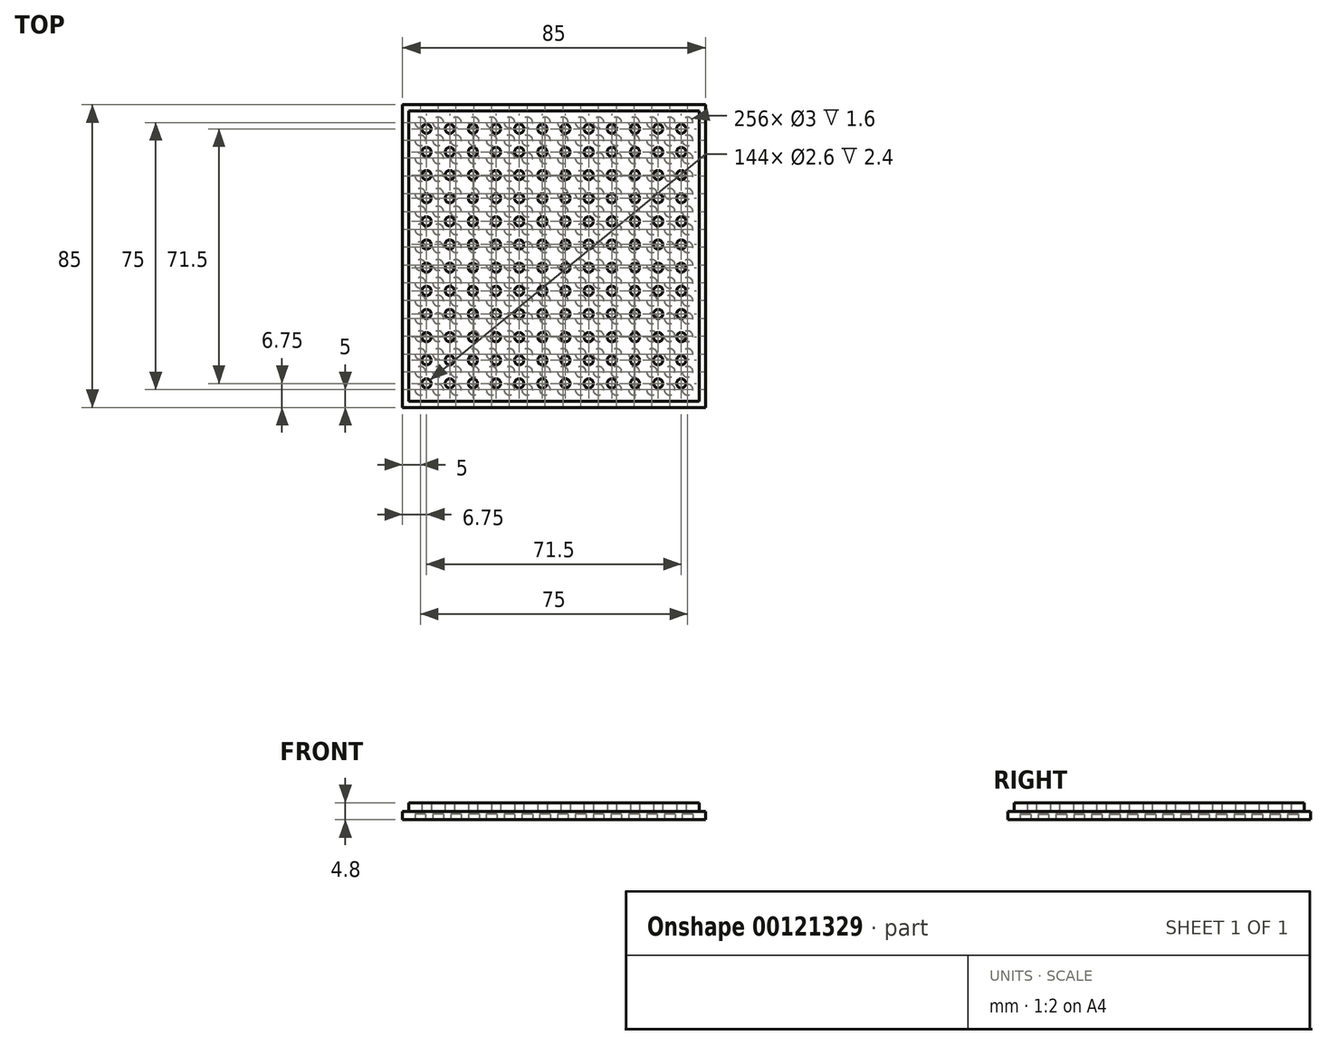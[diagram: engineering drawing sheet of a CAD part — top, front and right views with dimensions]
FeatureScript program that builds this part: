
annotation { "Feature Type Name" : "Feature", "Feature Type Description" : "" }
export const myFeature = defineFeature(function(context is Context, id is Id, definition is map)
    precondition{}
    {
        {
            var Q0;
            Q0=qCreatedBy(makeId("Top.planeOp"),FACE);
            var sketch = newSketch(context, id + "F0", { "sketchPlane" : qUnion([Q0])});
            skLineSegment(sketch, "E0.bottom", {"start": v(2.5, -2.5) * mm, "end": v(-2.5, -2.5) * mm, "construction": true});
            skLineSegment(sketch, "E0.top", {"start": v(2.5, 2.5) * mm, "end": v(-2.5, 2.5) * mm, "construction": true});
            skLineSegment(sketch, "E0.left", {"start": v(2.5, -2.5) * mm, "end": v(2.5, 2.5) * mm, "construction": true});
            skLineSegment(sketch, "E0.right", {"start": v(-2.5, -2.5) * mm, "end": v(-2.5, 2.5) * mm, "construction": true});
            skPoint(sketch, "E0.middle", {"position": v(0, 0) * mm});
            skCircle(sketch, "E1", {"center": v(-2.5, 2.5) * mm, "radius": 1.5 * mm});
            skCircle(sketch, "E2", {"center": v(2.5, 2.5) * mm, "radius": 1.5 * mm});
            skCircle(sketch, "E3", {"center": v(2.5, -2.5) * mm, "radius": 1.5 * mm});
            skCircle(sketch, "E4", {"center": v(-2.5, -2.5) * mm, "radius": 1.5 * mm});
            skPoint(sketch, "E5.0.1.0", {"position": v(0, 10) * mm});
            skLineSegment(sketch, "E5.0.1.1", {"start": v(-2.5, 7.5) * mm, "end": v(-2.5, 12.5) * mm, "construction": true});
            skLineSegment(sketch, "E5.0.1.2", {"start": v(2.5, 7.5) * mm, "end": v(2.5, 12.5) * mm, "construction": true});
            skLineSegment(sketch, "E5.0.1.3", {"start": v(2.5, 7.5) * mm, "end": v(-2.5, 7.5) * mm, "construction": true});
            skLineSegment(sketch, "E5.0.1.4", {"start": v(2.5, 12.5) * mm, "end": v(-2.5, 12.5) * mm, "construction": true});
            skCircle(sketch, "E5.0.1.5", {"center": v(-2.5, 7.5) * mm, "radius": 1.5 * mm});
            skCircle(sketch, "E5.0.1.6", {"center": v(2.5, 7.5) * mm, "radius": 1.5 * mm});
            skCircle(sketch, "E5.0.1.7", {"center": v(2.5, 12.5) * mm, "radius": 1.5 * mm});
            skCircle(sketch, "E5.0.1.8", {"center": v(-2.5, 12.5) * mm, "radius": 1.5 * mm});
            skPoint(sketch, "E5.0.2.0", {"position": v(0, 20) * mm});
            skLineSegment(sketch, "E5.0.2.1", {"start": v(-2.5, 17.5) * mm, "end": v(-2.5, 22.5) * mm, "construction": true});
            skLineSegment(sketch, "E5.0.2.2", {"start": v(2.5, 17.5) * mm, "end": v(2.5, 22.5) * mm, "construction": true});
            skLineSegment(sketch, "E5.0.2.3", {"start": v(2.5, 17.5) * mm, "end": v(-2.5, 17.5) * mm, "construction": true});
            skLineSegment(sketch, "E5.0.2.4", {"start": v(2.5, 22.5) * mm, "end": v(-2.5, 22.5) * mm, "construction": true});
            skCircle(sketch, "E5.0.2.5", {"center": v(-2.5, 17.5) * mm, "radius": 1.5 * mm});
            skCircle(sketch, "E5.0.2.6", {"center": v(2.5, 17.5) * mm, "radius": 1.5 * mm});
            skCircle(sketch, "E5.0.2.7", {"center": v(2.5, 22.5) * mm, "radius": 1.5 * mm});
            skCircle(sketch, "E5.0.2.8", {"center": v(-2.5, 22.5) * mm, "radius": 1.5 * mm});
            skPoint(sketch, "E5.0.3.0", {"position": v(0, 30) * mm});
            skLineSegment(sketch, "E5.0.3.1", {"start": v(-2.5, 27.5) * mm, "end": v(-2.5, 32.5) * mm, "construction": true});
            skLineSegment(sketch, "E5.0.3.2", {"start": v(2.5, 27.5) * mm, "end": v(2.5, 32.5) * mm, "construction": true});
            skLineSegment(sketch, "E5.0.3.3", {"start": v(2.5, 27.5) * mm, "end": v(-2.5, 27.5) * mm, "construction": true});
            skLineSegment(sketch, "E5.0.3.4", {"start": v(2.5, 32.5) * mm, "end": v(-2.5, 32.5) * mm, "construction": true});
            skCircle(sketch, "E5.0.3.5", {"center": v(-2.5, 27.5) * mm, "radius": 1.5 * mm});
            skCircle(sketch, "E5.0.3.6", {"center": v(2.5, 27.5) * mm, "radius": 1.5 * mm});
            skCircle(sketch, "E5.0.3.7", {"center": v(2.5, 32.5) * mm, "radius": 1.5 * mm});
            skCircle(sketch, "E5.0.3.8", {"center": v(-2.5, 32.5) * mm, "radius": 1.5 * mm});
            skPoint(sketch, "E5.0.4.0", {"position": v(0, 40) * mm});
            skLineSegment(sketch, "E5.0.4.1", {"start": v(-2.5, 37.5) * mm, "end": v(-2.5, 42.5) * mm, "construction": true});
            skLineSegment(sketch, "E5.0.4.2", {"start": v(2.5, 37.5) * mm, "end": v(2.5, 42.5) * mm, "construction": true});
            skLineSegment(sketch, "E5.0.4.3", {"start": v(2.5, 37.5) * mm, "end": v(-2.5, 37.5) * mm, "construction": true});
            skLineSegment(sketch, "E5.0.4.4", {"start": v(2.5, 42.5) * mm, "end": v(-2.5, 42.5) * mm, "construction": true});
            skCircle(sketch, "E5.0.4.5", {"center": v(-2.5, 37.5) * mm, "radius": 1.5 * mm});
            skCircle(sketch, "E5.0.4.6", {"center": v(2.5, 37.5) * mm, "radius": 1.5 * mm});
            skCircle(sketch, "E5.0.4.7", {"center": v(2.5, 42.5) * mm, "radius": 1.5 * mm});
            skCircle(sketch, "E5.0.4.8", {"center": v(-2.5, 42.5) * mm, "radius": 1.5 * mm});
            skPoint(sketch, "E5.0.5.0", {"position": v(0, 50) * mm});
            skLineSegment(sketch, "E5.0.5.1", {"start": v(-2.5, 47.5) * mm, "end": v(-2.5, 52.5) * mm, "construction": true});
            skLineSegment(sketch, "E5.0.5.2", {"start": v(2.5, 47.5) * mm, "end": v(2.5, 52.5) * mm, "construction": true});
            skLineSegment(sketch, "E5.0.5.3", {"start": v(2.5, 47.5) * mm, "end": v(-2.5, 47.5) * mm, "construction": true});
            skLineSegment(sketch, "E5.0.5.4", {"start": v(2.5, 52.5) * mm, "end": v(-2.5, 52.5) * mm, "construction": true});
            skCircle(sketch, "E5.0.5.5", {"center": v(-2.5, 47.5) * mm, "radius": 1.5 * mm});
            skCircle(sketch, "E5.0.5.6", {"center": v(2.5, 47.5) * mm, "radius": 1.5 * mm});
            skCircle(sketch, "E5.0.5.7", {"center": v(2.5, 52.5) * mm, "radius": 1.5 * mm});
            skCircle(sketch, "E5.0.5.8", {"center": v(-2.5, 52.5) * mm, "radius": 1.5 * mm});
            skPoint(sketch, "E5.1.0.0", {"position": v(10, 0) * mm});
            skLineSegment(sketch, "E5.1.0.1", {"start": v(7.5, -2.5) * mm, "end": v(7.5, 2.5) * mm, "construction": true});
            skLineSegment(sketch, "E5.1.0.2", {"start": v(12.5, -2.5) * mm, "end": v(12.5, 2.5) * mm, "construction": true});
            skLineSegment(sketch, "E5.1.0.3", {"start": v(12.5, -2.5) * mm, "end": v(7.5, -2.5) * mm, "construction": true});
            skLineSegment(sketch, "E5.1.0.4", {"start": v(12.5, 2.5) * mm, "end": v(7.5, 2.5) * mm, "construction": true});
            skCircle(sketch, "E5.1.0.5", {"center": v(7.5, -2.5) * mm, "radius": 1.5 * mm});
            skCircle(sketch, "E5.1.0.6", {"center": v(12.5, -2.5) * mm, "radius": 1.5 * mm});
            skCircle(sketch, "E5.1.0.7", {"center": v(12.5, 2.5) * mm, "radius": 1.5 * mm});
            skCircle(sketch, "E5.1.0.8", {"center": v(7.5, 2.5) * mm, "radius": 1.5 * mm});
            skPoint(sketch, "E5.1.1.0", {"position": v(10, 10) * mm});
            skLineSegment(sketch, "E5.1.1.1", {"start": v(7.5, 7.5) * mm, "end": v(7.5, 12.5) * mm, "construction": true});
            skLineSegment(sketch, "E5.1.1.2", {"start": v(12.5, 7.5) * mm, "end": v(12.5, 12.5) * mm, "construction": true});
            skLineSegment(sketch, "E5.1.1.3", {"start": v(12.5, 7.5) * mm, "end": v(7.5, 7.5) * mm, "construction": true});
            skLineSegment(sketch, "E5.1.1.4", {"start": v(12.5, 12.5) * mm, "end": v(7.5, 12.5) * mm, "construction": true});
            skCircle(sketch, "E5.1.1.5", {"center": v(7.5, 7.5) * mm, "radius": 1.5 * mm});
            skCircle(sketch, "E5.1.1.6", {"center": v(12.5, 7.5) * mm, "radius": 1.5 * mm});
            skCircle(sketch, "E5.1.1.7", {"center": v(12.5, 12.5) * mm, "radius": 1.5 * mm});
            skCircle(sketch, "E5.1.1.8", {"center": v(7.5, 12.5) * mm, "radius": 1.5 * mm});
            skPoint(sketch, "E5.1.2.0", {"position": v(10, 20) * mm});
            skLineSegment(sketch, "E5.1.2.1", {"start": v(7.5, 17.5) * mm, "end": v(7.5, 22.5) * mm, "construction": true});
            skLineSegment(sketch, "E5.1.2.2", {"start": v(12.5, 17.5) * mm, "end": v(12.5, 22.5) * mm, "construction": true});
            skLineSegment(sketch, "E5.1.2.3", {"start": v(12.5, 17.5) * mm, "end": v(7.5, 17.5) * mm, "construction": true});
            skLineSegment(sketch, "E5.1.2.4", {"start": v(12.5, 22.5) * mm, "end": v(7.5, 22.5) * mm, "construction": true});
            skCircle(sketch, "E5.1.2.5", {"center": v(7.5, 17.5) * mm, "radius": 1.5 * mm});
            skCircle(sketch, "E5.1.2.6", {"center": v(12.5, 17.5) * mm, "radius": 1.5 * mm});
            skCircle(sketch, "E5.1.2.7", {"center": v(12.5, 22.5) * mm, "radius": 1.5 * mm});
            skCircle(sketch, "E5.1.2.8", {"center": v(7.5, 22.5) * mm, "radius": 1.5 * mm});
            skPoint(sketch, "E5.1.3.0", {"position": v(10, 30) * mm});
            skLineSegment(sketch, "E5.1.3.1", {"start": v(7.5, 27.5) * mm, "end": v(7.5, 32.5) * mm, "construction": true});
            skLineSegment(sketch, "E5.1.3.2", {"start": v(12.5, 27.5) * mm, "end": v(12.5, 32.5) * mm, "construction": true});
            skLineSegment(sketch, "E5.1.3.3", {"start": v(12.5, 27.5) * mm, "end": v(7.5, 27.5) * mm, "construction": true});
            skLineSegment(sketch, "E5.1.3.4", {"start": v(12.5, 32.5) * mm, "end": v(7.5, 32.5) * mm, "construction": true});
            skCircle(sketch, "E5.1.3.5", {"center": v(7.5, 27.5) * mm, "radius": 1.5 * mm});
            skCircle(sketch, "E5.1.3.6", {"center": v(12.5, 27.5) * mm, "radius": 1.5 * mm});
            skCircle(sketch, "E5.1.3.7", {"center": v(12.5, 32.5) * mm, "radius": 1.5 * mm});
            skCircle(sketch, "E5.1.3.8", {"center": v(7.5, 32.5) * mm, "radius": 1.5 * mm});
            skPoint(sketch, "E5.1.4.0", {"position": v(10, 40) * mm});
            skLineSegment(sketch, "E5.1.4.1", {"start": v(7.5, 37.5) * mm, "end": v(7.5, 42.5) * mm, "construction": true});
            skLineSegment(sketch, "E5.1.4.2", {"start": v(12.5, 37.5) * mm, "end": v(12.5, 42.5) * mm, "construction": true});
            skLineSegment(sketch, "E5.1.4.3", {"start": v(12.5, 37.5) * mm, "end": v(7.5, 37.5) * mm, "construction": true});
            skLineSegment(sketch, "E5.1.4.4", {"start": v(12.5, 42.5) * mm, "end": v(7.5, 42.5) * mm, "construction": true});
            skCircle(sketch, "E5.1.4.5", {"center": v(7.5, 37.5) * mm, "radius": 1.5 * mm});
            skCircle(sketch, "E5.1.4.6", {"center": v(12.5, 37.5) * mm, "radius": 1.5 * mm});
            skCircle(sketch, "E5.1.4.7", {"center": v(12.5, 42.5) * mm, "radius": 1.5 * mm});
            skCircle(sketch, "E5.1.4.8", {"center": v(7.5, 42.5) * mm, "radius": 1.5 * mm});
            skPoint(sketch, "E5.1.5.0", {"position": v(10, 50) * mm});
            skLineSegment(sketch, "E5.1.5.1", {"start": v(7.5, 47.5) * mm, "end": v(7.5, 52.5) * mm, "construction": true});
            skLineSegment(sketch, "E5.1.5.2", {"start": v(12.5, 47.5) * mm, "end": v(12.5, 52.5) * mm, "construction": true});
            skLineSegment(sketch, "E5.1.5.3", {"start": v(12.5, 47.5) * mm, "end": v(7.5, 47.5) * mm, "construction": true});
            skLineSegment(sketch, "E5.1.5.4", {"start": v(12.5, 52.5) * mm, "end": v(7.5, 52.5) * mm, "construction": true});
            skCircle(sketch, "E5.1.5.5", {"center": v(7.5, 47.5) * mm, "radius": 1.5 * mm});
            skCircle(sketch, "E5.1.5.6", {"center": v(12.5, 47.5) * mm, "radius": 1.5 * mm});
            skCircle(sketch, "E5.1.5.7", {"center": v(12.5, 52.5) * mm, "radius": 1.5 * mm});
            skCircle(sketch, "E5.1.5.8", {"center": v(7.5, 52.5) * mm, "radius": 1.5 * mm});
            skPoint(sketch, "E5.2.0.0", {"position": v(20, 0) * mm});
            skLineSegment(sketch, "E5.2.0.1", {"start": v(17.5, -2.5) * mm, "end": v(17.5, 2.5) * mm, "construction": true});
            skLineSegment(sketch, "E5.2.0.2", {"start": v(22.5, -2.5) * mm, "end": v(22.5, 2.5) * mm, "construction": true});
            skLineSegment(sketch, "E5.2.0.3", {"start": v(22.5, -2.5) * mm, "end": v(17.5, -2.5) * mm, "construction": true});
            skLineSegment(sketch, "E5.2.0.4", {"start": v(22.5, 2.5) * mm, "end": v(17.5, 2.5) * mm, "construction": true});
            skCircle(sketch, "E5.2.0.5", {"center": v(17.5, -2.5) * mm, "radius": 1.5 * mm});
            skCircle(sketch, "E5.2.0.6", {"center": v(22.5, -2.5) * mm, "radius": 1.5 * mm});
            skCircle(sketch, "E5.2.0.7", {"center": v(22.5, 2.5) * mm, "radius": 1.5 * mm});
            skCircle(sketch, "E5.2.0.8", {"center": v(17.5, 2.5) * mm, "radius": 1.5 * mm});
            skPoint(sketch, "E5.2.1.0", {"position": v(20, 10) * mm});
            skLineSegment(sketch, "E5.2.1.1", {"start": v(17.5, 7.5) * mm, "end": v(17.5, 12.5) * mm, "construction": true});
            skLineSegment(sketch, "E5.2.1.2", {"start": v(22.5, 7.5) * mm, "end": v(22.5, 12.5) * mm, "construction": true});
            skLineSegment(sketch, "E5.2.1.3", {"start": v(22.5, 7.5) * mm, "end": v(17.5, 7.5) * mm, "construction": true});
            skLineSegment(sketch, "E5.2.1.4", {"start": v(22.5, 12.5) * mm, "end": v(17.5, 12.5) * mm, "construction": true});
            skCircle(sketch, "E5.2.1.5", {"center": v(17.5, 7.5) * mm, "radius": 1.5 * mm});
            skCircle(sketch, "E5.2.1.6", {"center": v(22.5, 7.5) * mm, "radius": 1.5 * mm});
            skCircle(sketch, "E5.2.1.7", {"center": v(22.5, 12.5) * mm, "radius": 1.5 * mm});
            skCircle(sketch, "E5.2.1.8", {"center": v(17.5, 12.5) * mm, "radius": 1.5 * mm});
            skPoint(sketch, "E5.2.2.0", {"position": v(20, 20) * mm});
            skLineSegment(sketch, "E5.2.2.1", {"start": v(17.5, 17.5) * mm, "end": v(17.5, 22.5) * mm, "construction": true});
            skLineSegment(sketch, "E5.2.2.2", {"start": v(22.5, 17.5) * mm, "end": v(22.5, 22.5) * mm, "construction": true});
            skLineSegment(sketch, "E5.2.2.3", {"start": v(22.5, 17.5) * mm, "end": v(17.5, 17.5) * mm, "construction": true});
            skLineSegment(sketch, "E5.2.2.4", {"start": v(22.5, 22.5) * mm, "end": v(17.5, 22.5) * mm, "construction": true});
            skCircle(sketch, "E5.2.2.5", {"center": v(17.5, 17.5) * mm, "radius": 1.5 * mm});
            skCircle(sketch, "E5.2.2.6", {"center": v(22.5, 17.5) * mm, "radius": 1.5 * mm});
            skCircle(sketch, "E5.2.2.7", {"center": v(22.5, 22.5) * mm, "radius": 1.5 * mm});
            skCircle(sketch, "E5.2.2.8", {"center": v(17.5, 22.5) * mm, "radius": 1.5 * mm});
            skPoint(sketch, "E5.2.3.0", {"position": v(20, 30) * mm});
            skLineSegment(sketch, "E5.2.3.1", {"start": v(17.5, 27.5) * mm, "end": v(17.5, 32.5) * mm, "construction": true});
            skLineSegment(sketch, "E5.2.3.2", {"start": v(22.5, 27.5) * mm, "end": v(22.5, 32.5) * mm, "construction": true});
            skLineSegment(sketch, "E5.2.3.3", {"start": v(22.5, 27.5) * mm, "end": v(17.5, 27.5) * mm, "construction": true});
            skLineSegment(sketch, "E5.2.3.4", {"start": v(22.5, 32.5) * mm, "end": v(17.5, 32.5) * mm, "construction": true});
            skCircle(sketch, "E5.2.3.5", {"center": v(17.5, 27.5) * mm, "radius": 1.5 * mm});
            skCircle(sketch, "E5.2.3.6", {"center": v(22.5, 27.5) * mm, "radius": 1.5 * mm});
            skCircle(sketch, "E5.2.3.7", {"center": v(22.5, 32.5) * mm, "radius": 1.5 * mm});
            skCircle(sketch, "E5.2.3.8", {"center": v(17.5, 32.5) * mm, "radius": 1.5 * mm});
            skPoint(sketch, "E5.2.4.0", {"position": v(20, 40) * mm});
            skLineSegment(sketch, "E5.2.4.1", {"start": v(17.5, 37.5) * mm, "end": v(17.5, 42.5) * mm, "construction": true});
            skLineSegment(sketch, "E5.2.4.2", {"start": v(22.5, 37.5) * mm, "end": v(22.5, 42.5) * mm, "construction": true});
            skLineSegment(sketch, "E5.2.4.3", {"start": v(22.5, 37.5) * mm, "end": v(17.5, 37.5) * mm, "construction": true});
            skLineSegment(sketch, "E5.2.4.4", {"start": v(22.5, 42.5) * mm, "end": v(17.5, 42.5) * mm, "construction": true});
            skCircle(sketch, "E5.2.4.5", {"center": v(17.5, 37.5) * mm, "radius": 1.5 * mm});
            skCircle(sketch, "E5.2.4.6", {"center": v(22.5, 37.5) * mm, "radius": 1.5 * mm});
            skCircle(sketch, "E5.2.4.7", {"center": v(22.5, 42.5) * mm, "radius": 1.5 * mm});
            skCircle(sketch, "E5.2.4.8", {"center": v(17.5, 42.5) * mm, "radius": 1.5 * mm});
            skPoint(sketch, "E5.2.5.0", {"position": v(20, 50) * mm});
            skLineSegment(sketch, "E5.2.5.1", {"start": v(17.5, 47.5) * mm, "end": v(17.5, 52.5) * mm, "construction": true});
            skLineSegment(sketch, "E5.2.5.2", {"start": v(22.5, 47.5) * mm, "end": v(22.5, 52.5) * mm, "construction": true});
            skLineSegment(sketch, "E5.2.5.3", {"start": v(22.5, 47.5) * mm, "end": v(17.5, 47.5) * mm, "construction": true});
            skLineSegment(sketch, "E5.2.5.4", {"start": v(22.5, 52.5) * mm, "end": v(17.5, 52.5) * mm, "construction": true});
            skCircle(sketch, "E5.2.5.5", {"center": v(17.5, 47.5) * mm, "radius": 1.5 * mm});
            skCircle(sketch, "E5.2.5.6", {"center": v(22.5, 47.5) * mm, "radius": 1.5 * mm});
            skCircle(sketch, "E5.2.5.7", {"center": v(22.5, 52.5) * mm, "radius": 1.5 * mm});
            skCircle(sketch, "E5.2.5.8", {"center": v(17.5, 52.5) * mm, "radius": 1.5 * mm});
            skPoint(sketch, "E5.3.0.0", {"position": v(30, 0) * mm});
            skLineSegment(sketch, "E5.3.0.1", {"start": v(27.5, -2.5) * mm, "end": v(27.5, 2.5) * mm, "construction": true});
            skLineSegment(sketch, "E5.3.0.2", {"start": v(32.5, -2.5) * mm, "end": v(32.5, 2.5) * mm, "construction": true});
            skLineSegment(sketch, "E5.3.0.3", {"start": v(32.5, -2.5) * mm, "end": v(27.5, -2.5) * mm, "construction": true});
            skLineSegment(sketch, "E5.3.0.4", {"start": v(32.5, 2.5) * mm, "end": v(27.5, 2.5) * mm, "construction": true});
            skCircle(sketch, "E5.3.0.5", {"center": v(27.5, -2.5) * mm, "radius": 1.5 * mm});
            skCircle(sketch, "E5.3.0.6", {"center": v(32.5, -2.5) * mm, "radius": 1.5 * mm});
            skCircle(sketch, "E5.3.0.7", {"center": v(32.5, 2.5) * mm, "radius": 1.5 * mm});
            skCircle(sketch, "E5.3.0.8", {"center": v(27.5, 2.5) * mm, "radius": 1.5 * mm});
            skPoint(sketch, "E5.3.1.0", {"position": v(30, 10) * mm});
            skLineSegment(sketch, "E5.3.1.1", {"start": v(27.5, 7.5) * mm, "end": v(27.5, 12.5) * mm, "construction": true});
            skLineSegment(sketch, "E5.3.1.2", {"start": v(32.5, 7.5) * mm, "end": v(32.5, 12.5) * mm, "construction": true});
            skLineSegment(sketch, "E5.3.1.3", {"start": v(32.5, 7.5) * mm, "end": v(27.5, 7.5) * mm, "construction": true});
            skLineSegment(sketch, "E5.3.1.4", {"start": v(32.5, 12.5) * mm, "end": v(27.5, 12.5) * mm, "construction": true});
            skCircle(sketch, "E5.3.1.5", {"center": v(27.5, 7.5) * mm, "radius": 1.5 * mm});
            skCircle(sketch, "E5.3.1.6", {"center": v(32.5, 7.5) * mm, "radius": 1.5 * mm});
            skCircle(sketch, "E5.3.1.7", {"center": v(32.5, 12.5) * mm, "radius": 1.5 * mm});
            skCircle(sketch, "E5.3.1.8", {"center": v(27.5, 12.5) * mm, "radius": 1.5 * mm});
            skPoint(sketch, "E5.3.2.0", {"position": v(30, 20) * mm});
            skLineSegment(sketch, "E5.3.2.1", {"start": v(27.5, 17.5) * mm, "end": v(27.5, 22.5) * mm, "construction": true});
            skLineSegment(sketch, "E5.3.2.2", {"start": v(32.5, 17.5) * mm, "end": v(32.5, 22.5) * mm, "construction": true});
            skLineSegment(sketch, "E5.3.2.3", {"start": v(32.5, 17.5) * mm, "end": v(27.5, 17.5) * mm, "construction": true});
            skLineSegment(sketch, "E5.3.2.4", {"start": v(32.5, 22.5) * mm, "end": v(27.5, 22.5) * mm, "construction": true});
            skCircle(sketch, "E5.3.2.5", {"center": v(27.5, 17.5) * mm, "radius": 1.5 * mm});
            skCircle(sketch, "E5.3.2.6", {"center": v(32.5, 17.5) * mm, "radius": 1.5 * mm});
            skCircle(sketch, "E5.3.2.7", {"center": v(32.5, 22.5) * mm, "radius": 1.5 * mm});
            skCircle(sketch, "E5.3.2.8", {"center": v(27.5, 22.5) * mm, "radius": 1.5 * mm});
            skPoint(sketch, "E5.3.3.0", {"position": v(30, 30) * mm});
            skLineSegment(sketch, "E5.3.3.1", {"start": v(27.5, 27.5) * mm, "end": v(27.5, 32.5) * mm, "construction": true});
            skLineSegment(sketch, "E5.3.3.2", {"start": v(32.5, 27.5) * mm, "end": v(32.5, 32.5) * mm, "construction": true});
            skLineSegment(sketch, "E5.3.3.3", {"start": v(32.5, 27.5) * mm, "end": v(27.5, 27.5) * mm, "construction": true});
            skLineSegment(sketch, "E5.3.3.4", {"start": v(32.5, 32.5) * mm, "end": v(27.5, 32.5) * mm, "construction": true});
            skCircle(sketch, "E5.3.3.5", {"center": v(27.5, 27.5) * mm, "radius": 1.5 * mm});
            skCircle(sketch, "E5.3.3.6", {"center": v(32.5, 27.5) * mm, "radius": 1.5 * mm});
            skCircle(sketch, "E5.3.3.7", {"center": v(32.5, 32.5) * mm, "radius": 1.5 * mm});
            skCircle(sketch, "E5.3.3.8", {"center": v(27.5, 32.5) * mm, "radius": 1.5 * mm});
            skPoint(sketch, "E5.3.4.0", {"position": v(30, 40) * mm});
            skLineSegment(sketch, "E5.3.4.1", {"start": v(27.5, 37.5) * mm, "end": v(27.5, 42.5) * mm, "construction": true});
            skLineSegment(sketch, "E5.3.4.2", {"start": v(32.5, 37.5) * mm, "end": v(32.5, 42.5) * mm, "construction": true});
            skLineSegment(sketch, "E5.3.4.3", {"start": v(32.5, 37.5) * mm, "end": v(27.5, 37.5) * mm, "construction": true});
            skLineSegment(sketch, "E5.3.4.4", {"start": v(32.5, 42.5) * mm, "end": v(27.5, 42.5) * mm, "construction": true});
            skCircle(sketch, "E5.3.4.5", {"center": v(27.5, 37.5) * mm, "radius": 1.5 * mm});
            skCircle(sketch, "E5.3.4.6", {"center": v(32.5, 37.5) * mm, "radius": 1.5 * mm});
            skCircle(sketch, "E5.3.4.7", {"center": v(32.5, 42.5) * mm, "radius": 1.5 * mm});
            skCircle(sketch, "E5.3.4.8", {"center": v(27.5, 42.5) * mm, "radius": 1.5 * mm});
            skPoint(sketch, "E5.3.5.0", {"position": v(30, 50) * mm});
            skLineSegment(sketch, "E5.3.5.1", {"start": v(27.5, 47.5) * mm, "end": v(27.5, 52.5) * mm, "construction": true});
            skLineSegment(sketch, "E5.3.5.2", {"start": v(32.5, 47.5) * mm, "end": v(32.5, 52.5) * mm, "construction": true});
            skLineSegment(sketch, "E5.3.5.3", {"start": v(32.5, 47.5) * mm, "end": v(27.5, 47.5) * mm, "construction": true});
            skLineSegment(sketch, "E5.3.5.4", {"start": v(32.5, 52.5) * mm, "end": v(27.5, 52.5) * mm, "construction": true});
            skCircle(sketch, "E5.3.5.5", {"center": v(27.5, 47.5) * mm, "radius": 1.5 * mm});
            skCircle(sketch, "E5.3.5.6", {"center": v(32.5, 47.5) * mm, "radius": 1.5 * mm});
            skCircle(sketch, "E5.3.5.7", {"center": v(32.5, 52.5) * mm, "radius": 1.5 * mm});
            skCircle(sketch, "E5.3.5.8", {"center": v(27.5, 52.5) * mm, "radius": 1.5 * mm});
            skPoint(sketch, "E5.4.0.0", {"position": v(40, 0) * mm});
            skLineSegment(sketch, "E5.4.0.1", {"start": v(37.5, -2.5) * mm, "end": v(37.5, 2.5) * mm, "construction": true});
            skLineSegment(sketch, "E5.4.0.2", {"start": v(42.5, -2.5) * mm, "end": v(42.5, 2.5) * mm, "construction": true});
            skLineSegment(sketch, "E5.4.0.3", {"start": v(42.5, -2.5) * mm, "end": v(37.5, -2.5) * mm, "construction": true});
            skLineSegment(sketch, "E5.4.0.4", {"start": v(42.5, 2.5) * mm, "end": v(37.5, 2.5) * mm, "construction": true});
            skCircle(sketch, "E5.4.0.5", {"center": v(37.5, -2.5) * mm, "radius": 1.5 * mm});
            skCircle(sketch, "E5.4.0.6", {"center": v(42.5, -2.5) * mm, "radius": 1.5 * mm});
            skCircle(sketch, "E5.4.0.7", {"center": v(42.5, 2.5) * mm, "radius": 1.5 * mm});
            skCircle(sketch, "E5.4.0.8", {"center": v(37.5, 2.5) * mm, "radius": 1.5 * mm});
            skPoint(sketch, "E5.4.1.0", {"position": v(40, 10) * mm});
            skLineSegment(sketch, "E5.4.1.1", {"start": v(37.5, 7.5) * mm, "end": v(37.5, 12.5) * mm, "construction": true});
            skLineSegment(sketch, "E5.4.1.2", {"start": v(42.5, 7.5) * mm, "end": v(42.5, 12.5) * mm, "construction": true});
            skLineSegment(sketch, "E5.4.1.3", {"start": v(42.5, 7.5) * mm, "end": v(37.5, 7.5) * mm, "construction": true});
            skLineSegment(sketch, "E5.4.1.4", {"start": v(42.5, 12.5) * mm, "end": v(37.5, 12.5) * mm, "construction": true});
            skCircle(sketch, "E5.4.1.5", {"center": v(37.5, 7.5) * mm, "radius": 1.5 * mm});
            skCircle(sketch, "E5.4.1.6", {"center": v(42.5, 7.5) * mm, "radius": 1.5 * mm});
            skCircle(sketch, "E5.4.1.7", {"center": v(42.5, 12.5) * mm, "radius": 1.5 * mm});
            skCircle(sketch, "E5.4.1.8", {"center": v(37.5, 12.5) * mm, "radius": 1.5 * mm});
            skPoint(sketch, "E5.4.2.0", {"position": v(40, 20) * mm});
            skLineSegment(sketch, "E5.4.2.1", {"start": v(37.5, 17.5) * mm, "end": v(37.5, 22.5) * mm, "construction": true});
            skLineSegment(sketch, "E5.4.2.2", {"start": v(42.5, 17.5) * mm, "end": v(42.5, 22.5) * mm, "construction": true});
            skLineSegment(sketch, "E5.4.2.3", {"start": v(42.5, 17.5) * mm, "end": v(37.5, 17.5) * mm, "construction": true});
            skLineSegment(sketch, "E5.4.2.4", {"start": v(42.5, 22.5) * mm, "end": v(37.5, 22.5) * mm, "construction": true});
            skCircle(sketch, "E5.4.2.5", {"center": v(37.5, 17.5) * mm, "radius": 1.5 * mm});
            skCircle(sketch, "E5.4.2.6", {"center": v(42.5, 17.5) * mm, "radius": 1.5 * mm});
            skCircle(sketch, "E5.4.2.7", {"center": v(42.5, 22.5) * mm, "radius": 1.5 * mm});
            skCircle(sketch, "E5.4.2.8", {"center": v(37.5, 22.5) * mm, "radius": 1.5 * mm});
            skPoint(sketch, "E5.4.3.0", {"position": v(40, 30) * mm});
            skLineSegment(sketch, "E5.4.3.1", {"start": v(37.5, 27.5) * mm, "end": v(37.5, 32.5) * mm, "construction": true});
            skLineSegment(sketch, "E5.4.3.2", {"start": v(42.5, 27.5) * mm, "end": v(42.5, 32.5) * mm, "construction": true});
            skLineSegment(sketch, "E5.4.3.3", {"start": v(42.5, 27.5) * mm, "end": v(37.5, 27.5) * mm, "construction": true});
            skLineSegment(sketch, "E5.4.3.4", {"start": v(42.5, 32.5) * mm, "end": v(37.5, 32.5) * mm, "construction": true});
            skCircle(sketch, "E5.4.3.5", {"center": v(37.5, 27.5) * mm, "radius": 1.5 * mm});
            skCircle(sketch, "E5.4.3.6", {"center": v(42.5, 27.5) * mm, "radius": 1.5 * mm});
            skCircle(sketch, "E5.4.3.7", {"center": v(42.5, 32.5) * mm, "radius": 1.5 * mm});
            skCircle(sketch, "E5.4.3.8", {"center": v(37.5, 32.5) * mm, "radius": 1.5 * mm});
            skPoint(sketch, "E5.4.4.0", {"position": v(40, 40) * mm});
            skLineSegment(sketch, "E5.4.4.1", {"start": v(37.5, 37.5) * mm, "end": v(37.5, 42.5) * mm, "construction": true});
            skLineSegment(sketch, "E5.4.4.2", {"start": v(42.5, 37.5) * mm, "end": v(42.5, 42.5) * mm, "construction": true});
            skLineSegment(sketch, "E5.4.4.3", {"start": v(42.5, 37.5) * mm, "end": v(37.5, 37.5) * mm, "construction": true});
            skLineSegment(sketch, "E5.4.4.4", {"start": v(42.5, 42.5) * mm, "end": v(37.5, 42.5) * mm, "construction": true});
            skCircle(sketch, "E5.4.4.5", {"center": v(37.5, 37.5) * mm, "radius": 1.5 * mm});
            skCircle(sketch, "E5.4.4.6", {"center": v(42.5, 37.5) * mm, "radius": 1.5 * mm});
            skCircle(sketch, "E5.4.4.7", {"center": v(42.5, 42.5) * mm, "radius": 1.5 * mm});
            skCircle(sketch, "E5.4.4.8", {"center": v(37.5, 42.5) * mm, "radius": 1.5 * mm});
            skPoint(sketch, "E5.4.5.0", {"position": v(40, 50) * mm});
            skLineSegment(sketch, "E5.4.5.1", {"start": v(37.5, 47.5) * mm, "end": v(37.5, 52.5) * mm, "construction": true});
            skLineSegment(sketch, "E5.4.5.2", {"start": v(42.5, 47.5) * mm, "end": v(42.5, 52.5) * mm, "construction": true});
            skLineSegment(sketch, "E5.4.5.3", {"start": v(42.5, 47.5) * mm, "end": v(37.5, 47.5) * mm, "construction": true});
            skLineSegment(sketch, "E5.4.5.4", {"start": v(42.5, 52.5) * mm, "end": v(37.5, 52.5) * mm, "construction": true});
            skCircle(sketch, "E5.4.5.5", {"center": v(37.5, 47.5) * mm, "radius": 1.5 * mm});
            skCircle(sketch, "E5.4.5.6", {"center": v(42.5, 47.5) * mm, "radius": 1.5 * mm});
            skCircle(sketch, "E5.4.5.7", {"center": v(42.5, 52.5) * mm, "radius": 1.5 * mm});
            skCircle(sketch, "E5.4.5.8", {"center": v(37.5, 52.5) * mm, "radius": 1.5 * mm});
            skPoint(sketch, "E5.5.0.0", {"position": v(50, 0) * mm});
            skLineSegment(sketch, "E5.5.0.1", {"start": v(47.5, -2.5) * mm, "end": v(47.5, 2.5) * mm, "construction": true});
            skLineSegment(sketch, "E5.5.0.2", {"start": v(52.5, -2.5) * mm, "end": v(52.5, 2.5) * mm, "construction": true});
            skLineSegment(sketch, "E5.5.0.3", {"start": v(52.5, -2.5) * mm, "end": v(47.5, -2.5) * mm, "construction": true});
            skLineSegment(sketch, "E5.5.0.4", {"start": v(52.5, 2.5) * mm, "end": v(47.5, 2.5) * mm, "construction": true});
            skCircle(sketch, "E5.5.0.5", {"center": v(47.5, -2.5) * mm, "radius": 1.5 * mm});
            skCircle(sketch, "E5.5.0.6", {"center": v(52.5, -2.5) * mm, "radius": 1.5 * mm});
            skCircle(sketch, "E5.5.0.7", {"center": v(52.5, 2.5) * mm, "radius": 1.5 * mm});
            skCircle(sketch, "E5.5.0.8", {"center": v(47.5, 2.5) * mm, "radius": 1.5 * mm});
            skPoint(sketch, "E5.5.1.0", {"position": v(50, 10) * mm});
            skLineSegment(sketch, "E5.5.1.1", {"start": v(47.5, 7.5) * mm, "end": v(47.5, 12.5) * mm, "construction": true});
            skLineSegment(sketch, "E5.5.1.2", {"start": v(52.5, 7.5) * mm, "end": v(52.5, 12.5) * mm, "construction": true});
            skLineSegment(sketch, "E5.5.1.3", {"start": v(52.5, 7.5) * mm, "end": v(47.5, 7.5) * mm, "construction": true});
            skLineSegment(sketch, "E5.5.1.4", {"start": v(52.5, 12.5) * mm, "end": v(47.5, 12.5) * mm, "construction": true});
            skCircle(sketch, "E5.5.1.5", {"center": v(47.5, 7.5) * mm, "radius": 1.5 * mm});
            skCircle(sketch, "E5.5.1.6", {"center": v(52.5, 7.5) * mm, "radius": 1.5 * mm});
            skCircle(sketch, "E5.5.1.7", {"center": v(52.5, 12.5) * mm, "radius": 1.5 * mm});
            skCircle(sketch, "E5.5.1.8", {"center": v(47.5, 12.5) * mm, "radius": 1.5 * mm});
            skPoint(sketch, "E5.5.2.0", {"position": v(50, 20) * mm});
            skLineSegment(sketch, "E5.5.2.1", {"start": v(47.5, 17.5) * mm, "end": v(47.5, 22.5) * mm, "construction": true});
            skLineSegment(sketch, "E5.5.2.2", {"start": v(52.5, 17.5) * mm, "end": v(52.5, 22.5) * mm, "construction": true});
            skLineSegment(sketch, "E5.5.2.3", {"start": v(52.5, 17.5) * mm, "end": v(47.5, 17.5) * mm, "construction": true});
            skLineSegment(sketch, "E5.5.2.4", {"start": v(52.5, 22.5) * mm, "end": v(47.5, 22.5) * mm, "construction": true});
            skCircle(sketch, "E5.5.2.5", {"center": v(47.5, 17.5) * mm, "radius": 1.5 * mm});
            skCircle(sketch, "E5.5.2.6", {"center": v(52.5, 17.5) * mm, "radius": 1.5 * mm});
            skCircle(sketch, "E5.5.2.7", {"center": v(52.5, 22.5) * mm, "radius": 1.5 * mm});
            skCircle(sketch, "E5.5.2.8", {"center": v(47.5, 22.5) * mm, "radius": 1.5 * mm});
            skPoint(sketch, "E5.5.3.0", {"position": v(50, 30) * mm});
            skLineSegment(sketch, "E5.5.3.1", {"start": v(47.5, 27.5) * mm, "end": v(47.5, 32.5) * mm, "construction": true});
            skLineSegment(sketch, "E5.5.3.2", {"start": v(52.5, 27.5) * mm, "end": v(52.5, 32.5) * mm, "construction": true});
            skLineSegment(sketch, "E5.5.3.3", {"start": v(52.5, 27.5) * mm, "end": v(47.5, 27.5) * mm, "construction": true});
            skLineSegment(sketch, "E5.5.3.4", {"start": v(52.5, 32.5) * mm, "end": v(47.5, 32.5) * mm, "construction": true});
            skCircle(sketch, "E5.5.3.5", {"center": v(47.5, 27.5) * mm, "radius": 1.5 * mm});
            skCircle(sketch, "E5.5.3.6", {"center": v(52.5, 27.5) * mm, "radius": 1.5 * mm});
            skCircle(sketch, "E5.5.3.7", {"center": v(52.5, 32.5) * mm, "radius": 1.5 * mm});
            skCircle(sketch, "E5.5.3.8", {"center": v(47.5, 32.5) * mm, "radius": 1.5 * mm});
            skPoint(sketch, "E5.5.4.0", {"position": v(50, 40) * mm});
            skLineSegment(sketch, "E5.5.4.1", {"start": v(47.5, 37.5) * mm, "end": v(47.5, 42.5) * mm, "construction": true});
            skLineSegment(sketch, "E5.5.4.2", {"start": v(52.5, 37.5) * mm, "end": v(52.5, 42.5) * mm, "construction": true});
            skLineSegment(sketch, "E5.5.4.3", {"start": v(52.5, 37.5) * mm, "end": v(47.5, 37.5) * mm, "construction": true});
            skLineSegment(sketch, "E5.5.4.4", {"start": v(52.5, 42.5) * mm, "end": v(47.5, 42.5) * mm, "construction": true});
            skCircle(sketch, "E5.5.4.5", {"center": v(47.5, 37.5) * mm, "radius": 1.5 * mm});
            skCircle(sketch, "E5.5.4.6", {"center": v(52.5, 37.5) * mm, "radius": 1.5 * mm});
            skCircle(sketch, "E5.5.4.7", {"center": v(52.5, 42.5) * mm, "radius": 1.5 * mm});
            skCircle(sketch, "E5.5.4.8", {"center": v(47.5, 42.5) * mm, "radius": 1.5 * mm});
            skPoint(sketch, "E5.5.5.0", {"position": v(50, 50) * mm});
            skLineSegment(sketch, "E5.5.5.1", {"start": v(47.5, 47.5) * mm, "end": v(47.5, 52.5) * mm, "construction": true});
            skLineSegment(sketch, "E5.5.5.2", {"start": v(52.5, 47.5) * mm, "end": v(52.5, 52.5) * mm, "construction": true});
            skLineSegment(sketch, "E5.5.5.3", {"start": v(52.5, 47.5) * mm, "end": v(47.5, 47.5) * mm, "construction": true});
            skLineSegment(sketch, "E5.5.5.4", {"start": v(52.5, 52.5) * mm, "end": v(47.5, 52.5) * mm, "construction": true});
            skCircle(sketch, "E5.5.5.5", {"center": v(47.5, 47.5) * mm, "radius": 1.5 * mm});
            skCircle(sketch, "E5.5.5.6", {"center": v(52.5, 47.5) * mm, "radius": 1.5 * mm});
            skCircle(sketch, "E5.5.5.7", {"center": v(52.5, 52.5) * mm, "radius": 1.5 * mm});
            skCircle(sketch, "E5.5.5.8", {"center": v(47.5, 52.5) * mm, "radius": 1.5 * mm});
            skLineSegment(sketch, "E5.direction1", {"start": v(-2.5, -2.5) * mm, "end": v(7.5, -2.5) * mm, "construction": true});
            skLineSegment(sketch, "E5.direction2", {"start": v(-2.5, -2.5) * mm, "end": v(-2.5, 7.5) * mm, "construction": true});
            skPoint(sketch, "E6.0.6.0", {"position": v(60, 0) * mm});
            skLineSegment(sketch, "E6.1.6.0", {"start": v(57.5, -2.5) * mm, "end": v(57.5, 2.5) * mm, "construction": true});
            skLineSegment(sketch, "E6.4.6.0", {"start": v(62.5, -2.5) * mm, "end": v(62.5, 2.5) * mm, "construction": true});
            skLineSegment(sketch, "E6.7.6.0", {"start": v(62.5, -2.5) * mm, "end": v(57.5, -2.5) * mm, "construction": true});
            skLineSegment(sketch, "E6.10.6.0", {"start": v(62.5, 2.5) * mm, "end": v(57.5, 2.5) * mm, "construction": true});
            skCircle(sketch, "E6.13.6.0", {"center": v(57.5, -2.5) * mm, "radius": 1.5 * mm});
            skCircle(sketch, "E6.15.6.0", {"center": v(62.5, -2.5) * mm, "radius": 1.5 * mm});
            skCircle(sketch, "E6.17.6.0", {"center": v(62.5, 2.5) * mm, "radius": 1.5 * mm});
            skCircle(sketch, "E6.19.6.0", {"center": v(57.5, 2.5) * mm, "radius": 1.5 * mm});
            skPoint(sketch, "E6.0.6.1", {"position": v(60, 10) * mm});
            skLineSegment(sketch, "E6.1.6.1", {"start": v(57.5, 7.5) * mm, "end": v(57.5, 12.5) * mm, "construction": true});
            skLineSegment(sketch, "E6.4.6.1", {"start": v(62.5, 7.5) * mm, "end": v(62.5, 12.5) * mm, "construction": true});
            skLineSegment(sketch, "E6.7.6.1", {"start": v(62.5, 7.5) * mm, "end": v(57.5, 7.5) * mm, "construction": true});
            skLineSegment(sketch, "E6.10.6.1", {"start": v(62.5, 12.5) * mm, "end": v(57.5, 12.5) * mm, "construction": true});
            skCircle(sketch, "E6.13.6.1", {"center": v(57.5, 7.5) * mm, "radius": 1.5 * mm});
            skCircle(sketch, "E6.15.6.1", {"center": v(62.5, 7.5) * mm, "radius": 1.5 * mm});
            skCircle(sketch, "E6.17.6.1", {"center": v(62.5, 12.5) * mm, "radius": 1.5 * mm});
            skCircle(sketch, "E6.19.6.1", {"center": v(57.5, 12.5) * mm, "radius": 1.5 * mm});
            skPoint(sketch, "E6.0.6.2", {"position": v(60, 20) * mm});
            skLineSegment(sketch, "E6.1.6.2", {"start": v(57.5, 17.5) * mm, "end": v(57.5, 22.5) * mm, "construction": true});
            skLineSegment(sketch, "E6.4.6.2", {"start": v(62.5, 17.5) * mm, "end": v(62.5, 22.5) * mm, "construction": true});
            skLineSegment(sketch, "E6.7.6.2", {"start": v(62.5, 17.5) * mm, "end": v(57.5, 17.5) * mm, "construction": true});
            skLineSegment(sketch, "E6.10.6.2", {"start": v(62.5, 22.5) * mm, "end": v(57.5, 22.5) * mm, "construction": true});
            skCircle(sketch, "E6.13.6.2", {"center": v(57.5, 17.5) * mm, "radius": 1.5 * mm});
            skCircle(sketch, "E6.15.6.2", {"center": v(62.5, 17.5) * mm, "radius": 1.5 * mm});
            skCircle(sketch, "E6.17.6.2", {"center": v(62.5, 22.5) * mm, "radius": 1.5 * mm});
            skCircle(sketch, "E6.19.6.2", {"center": v(57.5, 22.5) * mm, "radius": 1.5 * mm});
            skPoint(sketch, "E6.0.6.3", {"position": v(60, 30) * mm});
            skLineSegment(sketch, "E6.1.6.3", {"start": v(57.5, 27.5) * mm, "end": v(57.5, 32.5) * mm, "construction": true});
            skLineSegment(sketch, "E6.4.6.3", {"start": v(62.5, 27.5) * mm, "end": v(62.5, 32.5) * mm, "construction": true});
            skLineSegment(sketch, "E6.7.6.3", {"start": v(62.5, 27.5) * mm, "end": v(57.5, 27.5) * mm, "construction": true});
            skLineSegment(sketch, "E6.10.6.3", {"start": v(62.5, 32.5) * mm, "end": v(57.5, 32.5) * mm, "construction": true});
            skCircle(sketch, "E6.13.6.3", {"center": v(57.5, 27.5) * mm, "radius": 1.5 * mm});
            skCircle(sketch, "E6.15.6.3", {"center": v(62.5, 27.5) * mm, "radius": 1.5 * mm});
            skCircle(sketch, "E6.17.6.3", {"center": v(62.5, 32.5) * mm, "radius": 1.5 * mm});
            skCircle(sketch, "E6.19.6.3", {"center": v(57.5, 32.5) * mm, "radius": 1.5 * mm});
            skPoint(sketch, "E6.0.6.4", {"position": v(60, 40) * mm});
            skLineSegment(sketch, "E6.1.6.4", {"start": v(57.5, 37.5) * mm, "end": v(57.5, 42.5) * mm, "construction": true});
            skLineSegment(sketch, "E6.4.6.4", {"start": v(62.5, 37.5) * mm, "end": v(62.5, 42.5) * mm, "construction": true});
            skLineSegment(sketch, "E6.7.6.4", {"start": v(62.5, 37.5) * mm, "end": v(57.5, 37.5) * mm, "construction": true});
            skLineSegment(sketch, "E6.10.6.4", {"start": v(62.5, 42.5) * mm, "end": v(57.5, 42.5) * mm, "construction": true});
            skCircle(sketch, "E6.13.6.4", {"center": v(57.5, 37.5) * mm, "radius": 1.5 * mm});
            skCircle(sketch, "E6.15.6.4", {"center": v(62.5, 37.5) * mm, "radius": 1.5 * mm});
            skCircle(sketch, "E6.17.6.4", {"center": v(62.5, 42.5) * mm, "radius": 1.5 * mm});
            skCircle(sketch, "E6.19.6.4", {"center": v(57.5, 42.5) * mm, "radius": 1.5 * mm});
            skPoint(sketch, "E6.0.6.5", {"position": v(60, 50) * mm});
            skLineSegment(sketch, "E6.1.6.5", {"start": v(57.5, 47.5) * mm, "end": v(57.5, 52.5) * mm, "construction": true});
            skLineSegment(sketch, "E6.4.6.5", {"start": v(62.5, 47.5) * mm, "end": v(62.5, 52.5) * mm, "construction": true});
            skLineSegment(sketch, "E6.7.6.5", {"start": v(62.5, 47.5) * mm, "end": v(57.5, 47.5) * mm, "construction": true});
            skLineSegment(sketch, "E6.10.6.5", {"start": v(62.5, 52.5) * mm, "end": v(57.5, 52.5) * mm, "construction": true});
            skCircle(sketch, "E6.13.6.5", {"center": v(57.5, 47.5) * mm, "radius": 1.5 * mm});
            skCircle(sketch, "E6.15.6.5", {"center": v(62.5, 47.5) * mm, "radius": 1.5 * mm});
            skCircle(sketch, "E6.17.6.5", {"center": v(62.5, 52.5) * mm, "radius": 1.5 * mm});
            skCircle(sketch, "E6.19.6.5", {"center": v(57.5, 52.5) * mm, "radius": 1.5 * mm});
            skPoint(sketch, "E7.0.7.0", {"position": v(70, 0) * mm});
            skLineSegment(sketch, "E7.1.7.0", {"start": v(67.5, -2.5) * mm, "end": v(67.5, 2.5) * mm, "construction": true});
            skLineSegment(sketch, "E7.4.7.0", {"start": v(72.5, -2.5) * mm, "end": v(72.5, 2.5) * mm, "construction": true});
            skLineSegment(sketch, "E7.7.7.0", {"start": v(72.5, -2.5) * mm, "end": v(67.5, -2.5) * mm, "construction": true});
            skLineSegment(sketch, "E7.10.7.0", {"start": v(72.5, 2.5) * mm, "end": v(67.5, 2.5) * mm, "construction": true});
            skCircle(sketch, "E7.13.7.0", {"center": v(67.5, -2.5) * mm, "radius": 1.5 * mm});
            skCircle(sketch, "E7.15.7.0", {"center": v(72.5, -2.5) * mm, "radius": 1.5 * mm});
            skCircle(sketch, "E7.17.7.0", {"center": v(72.5, 2.5) * mm, "radius": 1.5 * mm});
            skCircle(sketch, "E7.19.7.0", {"center": v(67.5, 2.5) * mm, "radius": 1.5 * mm});
            skPoint(sketch, "E7.0.7.1", {"position": v(70, 10) * mm});
            skLineSegment(sketch, "E7.1.7.1", {"start": v(67.5, 7.5) * mm, "end": v(67.5, 12.5) * mm, "construction": true});
            skLineSegment(sketch, "E7.4.7.1", {"start": v(72.5, 7.5) * mm, "end": v(72.5, 12.5) * mm, "construction": true});
            skLineSegment(sketch, "E7.7.7.1", {"start": v(72.5, 7.5) * mm, "end": v(67.5, 7.5) * mm, "construction": true});
            skLineSegment(sketch, "E7.10.7.1", {"start": v(72.5, 12.5) * mm, "end": v(67.5, 12.5) * mm, "construction": true});
            skCircle(sketch, "E7.13.7.1", {"center": v(67.5, 7.5) * mm, "radius": 1.5 * mm});
            skCircle(sketch, "E7.15.7.1", {"center": v(72.5, 7.5) * mm, "radius": 1.5 * mm});
            skCircle(sketch, "E7.17.7.1", {"center": v(72.5, 12.5) * mm, "radius": 1.5 * mm});
            skCircle(sketch, "E7.19.7.1", {"center": v(67.5, 12.5) * mm, "radius": 1.5 * mm});
            skPoint(sketch, "E7.0.7.2", {"position": v(70, 20) * mm});
            skLineSegment(sketch, "E7.1.7.2", {"start": v(67.5, 17.5) * mm, "end": v(67.5, 22.5) * mm, "construction": true});
            skLineSegment(sketch, "E7.4.7.2", {"start": v(72.5, 17.5) * mm, "end": v(72.5, 22.5) * mm, "construction": true});
            skLineSegment(sketch, "E7.7.7.2", {"start": v(72.5, 17.5) * mm, "end": v(67.5, 17.5) * mm, "construction": true});
            skLineSegment(sketch, "E7.10.7.2", {"start": v(72.5, 22.5) * mm, "end": v(67.5, 22.5) * mm, "construction": true});
            skCircle(sketch, "E7.13.7.2", {"center": v(67.5, 17.5) * mm, "radius": 1.5 * mm});
            skCircle(sketch, "E7.15.7.2", {"center": v(72.5, 17.5) * mm, "radius": 1.5 * mm});
            skCircle(sketch, "E7.17.7.2", {"center": v(72.5, 22.5) * mm, "radius": 1.5 * mm});
            skCircle(sketch, "E7.19.7.2", {"center": v(67.5, 22.5) * mm, "radius": 1.5 * mm});
            skPoint(sketch, "E7.0.7.3", {"position": v(70, 30) * mm});
            skLineSegment(sketch, "E7.1.7.3", {"start": v(67.5, 27.5) * mm, "end": v(67.5, 32.5) * mm, "construction": true});
            skLineSegment(sketch, "E7.4.7.3", {"start": v(72.5, 27.5) * mm, "end": v(72.5, 32.5) * mm, "construction": true});
            skLineSegment(sketch, "E7.7.7.3", {"start": v(72.5, 27.5) * mm, "end": v(67.5, 27.5) * mm, "construction": true});
            skLineSegment(sketch, "E7.10.7.3", {"start": v(72.5, 32.5) * mm, "end": v(67.5, 32.5) * mm, "construction": true});
            skCircle(sketch, "E7.13.7.3", {"center": v(67.5, 27.5) * mm, "radius": 1.5 * mm});
            skCircle(sketch, "E7.15.7.3", {"center": v(72.5, 27.5) * mm, "radius": 1.5 * mm});
            skCircle(sketch, "E7.17.7.3", {"center": v(72.5, 32.5) * mm, "radius": 1.5 * mm});
            skCircle(sketch, "E7.19.7.3", {"center": v(67.5, 32.5) * mm, "radius": 1.5 * mm});
            skPoint(sketch, "E7.0.7.4", {"position": v(70, 40) * mm});
            skLineSegment(sketch, "E7.1.7.4", {"start": v(67.5, 37.5) * mm, "end": v(67.5, 42.5) * mm, "construction": true});
            skLineSegment(sketch, "E7.4.7.4", {"start": v(72.5, 37.5) * mm, "end": v(72.5, 42.5) * mm, "construction": true});
            skLineSegment(sketch, "E7.7.7.4", {"start": v(72.5, 37.5) * mm, "end": v(67.5, 37.5) * mm, "construction": true});
            skLineSegment(sketch, "E7.10.7.4", {"start": v(72.5, 42.5) * mm, "end": v(67.5, 42.5) * mm, "construction": true});
            skCircle(sketch, "E7.13.7.4", {"center": v(67.5, 37.5) * mm, "radius": 1.5 * mm});
            skCircle(sketch, "E7.15.7.4", {"center": v(72.5, 37.5) * mm, "radius": 1.5 * mm});
            skCircle(sketch, "E7.17.7.4", {"center": v(72.5, 42.5) * mm, "radius": 1.5 * mm});
            skCircle(sketch, "E7.19.7.4", {"center": v(67.5, 42.5) * mm, "radius": 1.5 * mm});
            skPoint(sketch, "E7.0.7.5", {"position": v(70, 50) * mm});
            skLineSegment(sketch, "E7.1.7.5", {"start": v(67.5, 47.5) * mm, "end": v(67.5, 52.5) * mm, "construction": true});
            skLineSegment(sketch, "E7.4.7.5", {"start": v(72.5, 47.5) * mm, "end": v(72.5, 52.5) * mm, "construction": true});
            skLineSegment(sketch, "E7.7.7.5", {"start": v(72.5, 47.5) * mm, "end": v(67.5, 47.5) * mm, "construction": true});
            skLineSegment(sketch, "E7.10.7.5", {"start": v(72.5, 52.5) * mm, "end": v(67.5, 52.5) * mm, "construction": true});
            skCircle(sketch, "E7.13.7.5", {"center": v(67.5, 47.5) * mm, "radius": 1.5 * mm});
            skCircle(sketch, "E7.15.7.5", {"center": v(72.5, 47.5) * mm, "radius": 1.5 * mm});
            skCircle(sketch, "E7.17.7.5", {"center": v(72.5, 52.5) * mm, "radius": 1.5 * mm});
            skCircle(sketch, "E7.19.7.5", {"center": v(67.5, 52.5) * mm, "radius": 1.5 * mm});
            skPoint(sketch, "E8.0.0.6", {"position": v(0, 60) * mm});
            skLineSegment(sketch, "E8.1.0.6", {"start": v(-2.5, 57.5) * mm, "end": v(-2.5, 62.5) * mm, "construction": true});
            skLineSegment(sketch, "E8.4.0.6", {"start": v(2.5, 57.5) * mm, "end": v(2.5, 62.5) * mm, "construction": true});
            skLineSegment(sketch, "E8.7.0.6", {"start": v(2.5, 57.5) * mm, "end": v(-2.5, 57.5) * mm, "construction": true});
            skLineSegment(sketch, "E8.10.0.6", {"start": v(2.5, 62.5) * mm, "end": v(-2.5, 62.5) * mm, "construction": true});
            skCircle(sketch, "E8.13.0.6", {"center": v(-2.5, 57.5) * mm, "radius": 1.5 * mm});
            skCircle(sketch, "E8.15.0.6", {"center": v(2.5, 57.5) * mm, "radius": 1.5 * mm});
            skCircle(sketch, "E8.17.0.6", {"center": v(2.5, 62.5) * mm, "radius": 1.5 * mm});
            skCircle(sketch, "E8.19.0.6", {"center": v(-2.5, 62.5) * mm, "radius": 1.5 * mm});
            skPoint(sketch, "E8.0.1.6", {"position": v(10, 60) * mm});
            skLineSegment(sketch, "E8.1.1.6", {"start": v(7.5, 57.5) * mm, "end": v(7.5, 62.5) * mm, "construction": true});
            skLineSegment(sketch, "E8.4.1.6", {"start": v(12.5, 57.5) * mm, "end": v(12.5, 62.5) * mm, "construction": true});
            skLineSegment(sketch, "E8.7.1.6", {"start": v(12.5, 57.5) * mm, "end": v(7.5, 57.5) * mm, "construction": true});
            skLineSegment(sketch, "E8.10.1.6", {"start": v(12.5, 62.5) * mm, "end": v(7.5, 62.5) * mm, "construction": true});
            skCircle(sketch, "E8.13.1.6", {"center": v(7.5, 57.5) * mm, "radius": 1.5 * mm});
            skCircle(sketch, "E8.15.1.6", {"center": v(12.5, 57.5) * mm, "radius": 1.5 * mm});
            skCircle(sketch, "E8.17.1.6", {"center": v(12.5, 62.5) * mm, "radius": 1.5 * mm});
            skCircle(sketch, "E8.19.1.6", {"center": v(7.5, 62.5) * mm, "radius": 1.5 * mm});
            skPoint(sketch, "E8.0.2.6", {"position": v(20, 60) * mm});
            skLineSegment(sketch, "E8.1.2.6", {"start": v(17.5, 57.5) * mm, "end": v(17.5, 62.5) * mm, "construction": true});
            skLineSegment(sketch, "E8.4.2.6", {"start": v(22.5, 57.5) * mm, "end": v(22.5, 62.5) * mm, "construction": true});
            skLineSegment(sketch, "E8.7.2.6", {"start": v(22.5, 57.5) * mm, "end": v(17.5, 57.5) * mm, "construction": true});
            skLineSegment(sketch, "E8.10.2.6", {"start": v(22.5, 62.5) * mm, "end": v(17.5, 62.5) * mm, "construction": true});
            skCircle(sketch, "E8.13.2.6", {"center": v(17.5, 57.5) * mm, "radius": 1.5 * mm});
            skCircle(sketch, "E8.15.2.6", {"center": v(22.5, 57.5) * mm, "radius": 1.5 * mm});
            skCircle(sketch, "E8.17.2.6", {"center": v(22.5, 62.5) * mm, "radius": 1.5 * mm});
            skCircle(sketch, "E8.19.2.6", {"center": v(17.5, 62.5) * mm, "radius": 1.5 * mm});
            skPoint(sketch, "E8.0.3.6", {"position": v(30, 60) * mm});
            skLineSegment(sketch, "E8.1.3.6", {"start": v(27.5, 57.5) * mm, "end": v(27.5, 62.5) * mm, "construction": true});
            skLineSegment(sketch, "E8.4.3.6", {"start": v(32.5, 57.5) * mm, "end": v(32.5, 62.5) * mm, "construction": true});
            skLineSegment(sketch, "E8.7.3.6", {"start": v(32.5, 57.5) * mm, "end": v(27.5, 57.5) * mm, "construction": true});
            skLineSegment(sketch, "E8.10.3.6", {"start": v(32.5, 62.5) * mm, "end": v(27.5, 62.5) * mm, "construction": true});
            skCircle(sketch, "E8.13.3.6", {"center": v(27.5, 57.5) * mm, "radius": 1.5 * mm});
            skCircle(sketch, "E8.15.3.6", {"center": v(32.5, 57.5) * mm, "radius": 1.5 * mm});
            skCircle(sketch, "E8.17.3.6", {"center": v(32.5, 62.5) * mm, "radius": 1.5 * mm});
            skCircle(sketch, "E8.19.3.6", {"center": v(27.5, 62.5) * mm, "radius": 1.5 * mm});
            skPoint(sketch, "E8.0.4.6", {"position": v(40, 60) * mm});
            skLineSegment(sketch, "E8.1.4.6", {"start": v(37.5, 57.5) * mm, "end": v(37.5, 62.5) * mm, "construction": true});
            skLineSegment(sketch, "E8.4.4.6", {"start": v(42.5, 57.5) * mm, "end": v(42.5, 62.5) * mm, "construction": true});
            skLineSegment(sketch, "E8.7.4.6", {"start": v(42.5, 57.5) * mm, "end": v(37.5, 57.5) * mm, "construction": true});
            skLineSegment(sketch, "E8.10.4.6", {"start": v(42.5, 62.5) * mm, "end": v(37.5, 62.5) * mm, "construction": true});
            skCircle(sketch, "E8.13.4.6", {"center": v(37.5, 57.5) * mm, "radius": 1.5 * mm});
            skCircle(sketch, "E8.15.4.6", {"center": v(42.5, 57.5) * mm, "radius": 1.5 * mm});
            skCircle(sketch, "E8.17.4.6", {"center": v(42.5, 62.5) * mm, "radius": 1.5 * mm});
            skCircle(sketch, "E8.19.4.6", {"center": v(37.5, 62.5) * mm, "radius": 1.5 * mm});
            skPoint(sketch, "E8.0.5.6", {"position": v(50, 60) * mm});
            skLineSegment(sketch, "E8.1.5.6", {"start": v(47.5, 57.5) * mm, "end": v(47.5, 62.5) * mm, "construction": true});
            skLineSegment(sketch, "E8.4.5.6", {"start": v(52.5, 57.5) * mm, "end": v(52.5, 62.5) * mm, "construction": true});
            skLineSegment(sketch, "E8.7.5.6", {"start": v(52.5, 57.5) * mm, "end": v(47.5, 57.5) * mm, "construction": true});
            skLineSegment(sketch, "E8.10.5.6", {"start": v(52.5, 62.5) * mm, "end": v(47.5, 62.5) * mm, "construction": true});
            skCircle(sketch, "E8.13.5.6", {"center": v(47.5, 57.5) * mm, "radius": 1.5 * mm});
            skCircle(sketch, "E8.15.5.6", {"center": v(52.5, 57.5) * mm, "radius": 1.5 * mm});
            skCircle(sketch, "E8.17.5.6", {"center": v(52.5, 62.5) * mm, "radius": 1.5 * mm});
            skCircle(sketch, "E8.19.5.6", {"center": v(47.5, 62.5) * mm, "radius": 1.5 * mm});
            skPoint(sketch, "E8.0.6.6", {"position": v(60, 60) * mm});
            skLineSegment(sketch, "E8.1.6.6", {"start": v(57.5, 57.5) * mm, "end": v(57.5, 62.5) * mm, "construction": true});
            skLineSegment(sketch, "E8.4.6.6", {"start": v(62.5, 57.5) * mm, "end": v(62.5, 62.5) * mm, "construction": true});
            skLineSegment(sketch, "E8.7.6.6", {"start": v(62.5, 57.5) * mm, "end": v(57.5, 57.5) * mm, "construction": true});
            skLineSegment(sketch, "E8.10.6.6", {"start": v(62.5, 62.5) * mm, "end": v(57.5, 62.5) * mm, "construction": true});
            skCircle(sketch, "E8.13.6.6", {"center": v(57.5, 57.5) * mm, "radius": 1.5 * mm});
            skCircle(sketch, "E8.15.6.6", {"center": v(62.5, 57.5) * mm, "radius": 1.5 * mm});
            skCircle(sketch, "E8.17.6.6", {"center": v(62.5, 62.5) * mm, "radius": 1.5 * mm});
            skCircle(sketch, "E8.19.6.6", {"center": v(57.5, 62.5) * mm, "radius": 1.5 * mm});
            skPoint(sketch, "E8.0.7.6", {"position": v(70, 60) * mm});
            skLineSegment(sketch, "E8.1.7.6", {"start": v(67.5, 57.5) * mm, "end": v(67.5, 62.5) * mm, "construction": true});
            skLineSegment(sketch, "E8.4.7.6", {"start": v(72.5, 57.5) * mm, "end": v(72.5, 62.5) * mm, "construction": true});
            skLineSegment(sketch, "E8.7.7.6", {"start": v(72.5, 57.5) * mm, "end": v(67.5, 57.5) * mm, "construction": true});
            skLineSegment(sketch, "E8.10.7.6", {"start": v(72.5, 62.5) * mm, "end": v(67.5, 62.5) * mm, "construction": true});
            skCircle(sketch, "E8.13.7.6", {"center": v(67.5, 57.5) * mm, "radius": 1.5 * mm});
            skCircle(sketch, "E8.15.7.6", {"center": v(72.5, 57.5) * mm, "radius": 1.5 * mm});
            skCircle(sketch, "E8.17.7.6", {"center": v(72.5, 62.5) * mm, "radius": 1.5 * mm});
            skCircle(sketch, "E8.19.7.6", {"center": v(67.5, 62.5) * mm, "radius": 1.5 * mm});
            skPoint(sketch, "E9.0.0.7", {"position": v(0, 70) * mm});
            skLineSegment(sketch, "E9.1.0.7", {"start": v(-2.5, 67.5) * mm, "end": v(-2.5, 72.5) * mm, "construction": true});
            skLineSegment(sketch, "E9.4.0.7", {"start": v(2.5, 67.5) * mm, "end": v(2.5, 72.5) * mm, "construction": true});
            skLineSegment(sketch, "E9.7.0.7", {"start": v(2.5, 67.5) * mm, "end": v(-2.5, 67.5) * mm, "construction": true});
            skLineSegment(sketch, "E9.10.0.7", {"start": v(2.5, 72.5) * mm, "end": v(-2.5, 72.5) * mm, "construction": true});
            skCircle(sketch, "E9.13.0.7", {"center": v(-2.5, 67.5) * mm, "radius": 1.5 * mm});
            skCircle(sketch, "E9.15.0.7", {"center": v(2.5, 67.5) * mm, "radius": 1.5 * mm});
            skCircle(sketch, "E9.17.0.7", {"center": v(2.5, 72.5) * mm, "radius": 1.5 * mm});
            skCircle(sketch, "E9.19.0.7", {"center": v(-2.5, 72.5) * mm, "radius": 1.5 * mm});
            skPoint(sketch, "E9.0.1.7", {"position": v(10, 70) * mm});
            skLineSegment(sketch, "E9.1.1.7", {"start": v(7.5, 67.5) * mm, "end": v(7.5, 72.5) * mm, "construction": true});
            skLineSegment(sketch, "E9.4.1.7", {"start": v(12.5, 67.5) * mm, "end": v(12.5, 72.5) * mm, "construction": true});
            skLineSegment(sketch, "E9.7.1.7", {"start": v(12.5, 67.5) * mm, "end": v(7.5, 67.5) * mm, "construction": true});
            skLineSegment(sketch, "E9.10.1.7", {"start": v(12.5, 72.5) * mm, "end": v(7.5, 72.5) * mm, "construction": true});
            skCircle(sketch, "E9.13.1.7", {"center": v(7.5, 67.5) * mm, "radius": 1.5 * mm});
            skCircle(sketch, "E9.15.1.7", {"center": v(12.5, 67.5) * mm, "radius": 1.5 * mm});
            skCircle(sketch, "E9.17.1.7", {"center": v(12.5, 72.5) * mm, "radius": 1.5 * mm});
            skCircle(sketch, "E9.19.1.7", {"center": v(7.5, 72.5) * mm, "radius": 1.5 * mm});
            skPoint(sketch, "E9.0.2.7", {"position": v(20, 70) * mm});
            skLineSegment(sketch, "E9.1.2.7", {"start": v(17.5, 67.5) * mm, "end": v(17.5, 72.5) * mm, "construction": true});
            skLineSegment(sketch, "E9.4.2.7", {"start": v(22.5, 67.5) * mm, "end": v(22.5, 72.5) * mm, "construction": true});
            skLineSegment(sketch, "E9.7.2.7", {"start": v(22.5, 67.5) * mm, "end": v(17.5, 67.5) * mm, "construction": true});
            skLineSegment(sketch, "E9.10.2.7", {"start": v(22.5, 72.5) * mm, "end": v(17.5, 72.5) * mm, "construction": true});
            skCircle(sketch, "E9.13.2.7", {"center": v(17.5, 67.5) * mm, "radius": 1.5 * mm});
            skCircle(sketch, "E9.15.2.7", {"center": v(22.5, 67.5) * mm, "radius": 1.5 * mm});
            skCircle(sketch, "E9.17.2.7", {"center": v(22.5, 72.5) * mm, "radius": 1.5 * mm});
            skCircle(sketch, "E9.19.2.7", {"center": v(17.5, 72.5) * mm, "radius": 1.5 * mm});
            skPoint(sketch, "E9.0.3.7", {"position": v(30, 70) * mm});
            skLineSegment(sketch, "E9.1.3.7", {"start": v(27.5, 67.5) * mm, "end": v(27.5, 72.5) * mm, "construction": true});
            skLineSegment(sketch, "E9.4.3.7", {"start": v(32.5, 67.5) * mm, "end": v(32.5, 72.5) * mm, "construction": true});
            skLineSegment(sketch, "E9.7.3.7", {"start": v(32.5, 67.5) * mm, "end": v(27.5, 67.5) * mm, "construction": true});
            skLineSegment(sketch, "E9.10.3.7", {"start": v(32.5, 72.5) * mm, "end": v(27.5, 72.5) * mm, "construction": true});
            skCircle(sketch, "E9.13.3.7", {"center": v(27.5, 67.5) * mm, "radius": 1.5 * mm});
            skCircle(sketch, "E9.15.3.7", {"center": v(32.5, 67.5) * mm, "radius": 1.5 * mm});
            skCircle(sketch, "E9.17.3.7", {"center": v(32.5, 72.5) * mm, "radius": 1.5 * mm});
            skCircle(sketch, "E9.19.3.7", {"center": v(27.5, 72.5) * mm, "radius": 1.5 * mm});
            skPoint(sketch, "E9.0.4.7", {"position": v(40, 70) * mm});
            skLineSegment(sketch, "E9.1.4.7", {"start": v(37.5, 67.5) * mm, "end": v(37.5, 72.5) * mm, "construction": true});
            skLineSegment(sketch, "E9.4.4.7", {"start": v(42.5, 67.5) * mm, "end": v(42.5, 72.5) * mm, "construction": true});
            skLineSegment(sketch, "E9.7.4.7", {"start": v(42.5, 67.5) * mm, "end": v(37.5, 67.5) * mm, "construction": true});
            skLineSegment(sketch, "E9.10.4.7", {"start": v(42.5, 72.5) * mm, "end": v(37.5, 72.5) * mm, "construction": true});
            skCircle(sketch, "E9.13.4.7", {"center": v(37.5, 67.5) * mm, "radius": 1.5 * mm});
            skCircle(sketch, "E9.15.4.7", {"center": v(42.5, 67.5) * mm, "radius": 1.5 * mm});
            skCircle(sketch, "E9.17.4.7", {"center": v(42.5, 72.5) * mm, "radius": 1.5 * mm});
            skCircle(sketch, "E9.19.4.7", {"center": v(37.5, 72.5) * mm, "radius": 1.5 * mm});
            skPoint(sketch, "E9.0.5.7", {"position": v(50, 70) * mm});
            skLineSegment(sketch, "E9.1.5.7", {"start": v(47.5, 67.5) * mm, "end": v(47.5, 72.5) * mm, "construction": true});
            skLineSegment(sketch, "E9.4.5.7", {"start": v(52.5, 67.5) * mm, "end": v(52.5, 72.5) * mm, "construction": true});
            skLineSegment(sketch, "E9.7.5.7", {"start": v(52.5, 67.5) * mm, "end": v(47.5, 67.5) * mm, "construction": true});
            skLineSegment(sketch, "E9.10.5.7", {"start": v(52.5, 72.5) * mm, "end": v(47.5, 72.5) * mm, "construction": true});
            skCircle(sketch, "E9.13.5.7", {"center": v(47.5, 67.5) * mm, "radius": 1.5 * mm});
            skCircle(sketch, "E9.15.5.7", {"center": v(52.5, 67.5) * mm, "radius": 1.5 * mm});
            skCircle(sketch, "E9.17.5.7", {"center": v(52.5, 72.5) * mm, "radius": 1.5 * mm});
            skCircle(sketch, "E9.19.5.7", {"center": v(47.5, 72.5) * mm, "radius": 1.5 * mm});
            skPoint(sketch, "E9.0.6.7", {"position": v(60, 70) * mm});
            skLineSegment(sketch, "E9.1.6.7", {"start": v(57.5, 67.5) * mm, "end": v(57.5, 72.5) * mm, "construction": true});
            skLineSegment(sketch, "E9.4.6.7", {"start": v(62.5, 67.5) * mm, "end": v(62.5, 72.5) * mm, "construction": true});
            skLineSegment(sketch, "E9.7.6.7", {"start": v(62.5, 67.5) * mm, "end": v(57.5, 67.5) * mm, "construction": true});
            skLineSegment(sketch, "E9.10.6.7", {"start": v(62.5, 72.5) * mm, "end": v(57.5, 72.5) * mm, "construction": true});
            skCircle(sketch, "E9.13.6.7", {"center": v(57.5, 67.5) * mm, "radius": 1.5 * mm});
            skCircle(sketch, "E9.15.6.7", {"center": v(62.5, 67.5) * mm, "radius": 1.5 * mm});
            skCircle(sketch, "E9.17.6.7", {"center": v(62.5, 72.5) * mm, "radius": 1.5 * mm});
            skCircle(sketch, "E9.19.6.7", {"center": v(57.5, 72.5) * mm, "radius": 1.5 * mm});
            skPoint(sketch, "E9.0.7.7", {"position": v(70, 70) * mm});
            skLineSegment(sketch, "E9.1.7.7", {"start": v(67.5, 67.5) * mm, "end": v(67.5, 72.5) * mm, "construction": true});
            skLineSegment(sketch, "E9.4.7.7", {"start": v(72.5, 67.5) * mm, "end": v(72.5, 72.5) * mm, "construction": true});
            skLineSegment(sketch, "E9.7.7.7", {"start": v(72.5, 67.5) * mm, "end": v(67.5, 67.5) * mm, "construction": true});
            skLineSegment(sketch, "E9.10.7.7", {"start": v(72.5, 72.5) * mm, "end": v(67.5, 72.5) * mm, "construction": true});
            skCircle(sketch, "E9.13.7.7", {"center": v(67.5, 67.5) * mm, "radius": 1.5 * mm});
            skCircle(sketch, "E9.15.7.7", {"center": v(72.5, 67.5) * mm, "radius": 1.5 * mm});
            skCircle(sketch, "E9.17.7.7", {"center": v(72.5, 72.5) * mm, "radius": 1.5 * mm});
            skCircle(sketch, "E9.19.7.7", {"center": v(67.5, 72.5) * mm, "radius": 1.5 * mm});
            skLineSegment(sketch, "E10.bottom", {"start": v(-7.5, -7.5) * mm, "end": v(77.5, -7.5) * mm});
            skLineSegment(sketch, "E10.top", {"start": v(-7.5, 77.5) * mm, "end": v(77.5, 77.5) * mm});
            skLineSegment(sketch, "E10.left", {"start": v(-7.5, -7.5) * mm, "end": v(-7.5, 77.5) * mm});
            skLineSegment(sketch, "E10.right", {"start": v(77.5, -7.5) * mm, "end": v(77.5, 77.5) * mm});
            skSolve(sketch);
        }
        {
            var Q0;
            Q0=makeQuery(id+"F0.imprint","IMPRINT",FACE,{"disambiguationData":[TD([[makeQuery(id+"F0.imprint","IMPRINT",EDGE,{"derivedFrom":sQuery(id+"F0.wireOp",EDGE,"E1")}),-1.0]])]});
            extrude(context, id + "F1", {"entities" : qUnion([Q0]), "depth" : 2.4 * mm});
        }
        {
            var Q0;
            Q0=makeQuery(id+"F1.opExtrude","CAP_FACE",FACE,{"disambiguationData":[OSD([sQuery(id+"F0.wireOp",EDGE,"E1"),sQuery(id+"F0.wireOp",EDGE,"E2"),sQuery(id+"F0.wireOp",EDGE,"E3"),sQuery(id+"F0.wireOp",EDGE,"E4"),sQuery(id+"F0.wireOp",EDGE,"E5.0.1.5"),sQuery(id+"F0.wireOp",EDGE,"E5.0.1.6"),sQuery(id+"F0.wireOp",EDGE,"E5.0.1.7"),sQuery(id+"F0.wireOp",EDGE,"E5.0.1.8"),sQuery(id+"F0.wireOp",EDGE,"E5.0.2.5"),sQuery(id+"F0.wireOp",EDGE,"E5.0.2.6"),sQuery(id+"F0.wireOp",EDGE,"E5.0.2.7"),sQuery(id+"F0.wireOp",EDGE,"E5.0.2.8"),sQuery(id+"F0.wireOp",EDGE,"E5.0.3.5"),sQuery(id+"F0.wireOp",EDGE,"E5.0.3.6"),sQuery(id+"F0.wireOp",EDGE,"E5.0.3.7"),sQuery(id+"F0.wireOp",EDGE,"E5.0.3.8"),sQuery(id+"F0.wireOp",EDGE,"E5.0.4.5"),sQuery(id+"F0.wireOp",EDGE,"E5.0.4.6"),sQuery(id+"F0.wireOp",EDGE,"E5.0.4.7"),sQuery(id+"F0.wireOp",EDGE,"E5.0.4.8"),sQuery(id+"F0.wireOp",EDGE,"E5.0.5.5"),sQuery(id+"F0.wireOp",EDGE,"E5.0.5.6"),sQuery(id+"F0.wireOp",EDGE,"E5.0.5.7"),sQuery(id+"F0.wireOp",EDGE,"E5.0.5.8"),sQuery(id+"F0.wireOp",EDGE,"E5.1.0.5"),sQuery(id+"F0.wireOp",EDGE,"E5.1.0.6"),sQuery(id+"F0.wireOp",EDGE,"E5.1.0.7"),sQuery(id+"F0.wireOp",EDGE,"E5.1.0.8"),sQuery(id+"F0.wireOp",EDGE,"E5.1.1.5"),sQuery(id+"F0.wireOp",EDGE,"E5.1.1.6"),sQuery(id+"F0.wireOp",EDGE,"E5.1.1.7"),sQuery(id+"F0.wireOp",EDGE,"E5.1.1.8"),sQuery(id+"F0.wireOp",EDGE,"E5.1.2.5"),sQuery(id+"F0.wireOp",EDGE,"E5.1.2.6"),sQuery(id+"F0.wireOp",EDGE,"E5.1.2.7"),sQuery(id+"F0.wireOp",EDGE,"E5.1.2.8"),sQuery(id+"F0.wireOp",EDGE,"E5.1.3.5"),sQuery(id+"F0.wireOp",EDGE,"E5.1.3.6"),sQuery(id+"F0.wireOp",EDGE,"E5.1.3.7"),sQuery(id+"F0.wireOp",EDGE,"E5.1.3.8"),sQuery(id+"F0.wireOp",EDGE,"E5.1.4.5"),sQuery(id+"F0.wireOp",EDGE,"E5.1.4.6"),sQuery(id+"F0.wireOp",EDGE,"E5.1.4.7"),sQuery(id+"F0.wireOp",EDGE,"E5.1.4.8"),sQuery(id+"F0.wireOp",EDGE,"E5.1.5.5"),sQuery(id+"F0.wireOp",EDGE,"E5.1.5.6"),sQuery(id+"F0.wireOp",EDGE,"E5.1.5.7"),sQuery(id+"F0.wireOp",EDGE,"E5.1.5.8"),sQuery(id+"F0.wireOp",EDGE,"E5.2.0.5"),sQuery(id+"F0.wireOp",EDGE,"E5.2.0.6"),sQuery(id+"F0.wireOp",EDGE,"E5.2.0.7"),sQuery(id+"F0.wireOp",EDGE,"E5.2.0.8"),sQuery(id+"F0.wireOp",EDGE,"E5.2.1.5"),sQuery(id+"F0.wireOp",EDGE,"E5.2.1.6"),sQuery(id+"F0.wireOp",EDGE,"E5.2.1.7"),sQuery(id+"F0.wireOp",EDGE,"E5.2.1.8"),sQuery(id+"F0.wireOp",EDGE,"E5.2.2.5"),sQuery(id+"F0.wireOp",EDGE,"E5.2.2.6"),sQuery(id+"F0.wireOp",EDGE,"E5.2.2.7"),sQuery(id+"F0.wireOp",EDGE,"E5.2.2.8"),sQuery(id+"F0.wireOp",EDGE,"E5.2.3.5"),sQuery(id+"F0.wireOp",EDGE,"E5.2.3.6"),sQuery(id+"F0.wireOp",EDGE,"E5.2.3.7"),sQuery(id+"F0.wireOp",EDGE,"E5.2.3.8"),sQuery(id+"F0.wireOp",EDGE,"E5.2.4.5"),sQuery(id+"F0.wireOp",EDGE,"E5.2.4.6"),sQuery(id+"F0.wireOp",EDGE,"E5.2.4.7"),sQuery(id+"F0.wireOp",EDGE,"E5.2.4.8"),sQuery(id+"F0.wireOp",EDGE,"E5.2.5.5"),sQuery(id+"F0.wireOp",EDGE,"E5.2.5.6"),sQuery(id+"F0.wireOp",EDGE,"E5.2.5.7"),sQuery(id+"F0.wireOp",EDGE,"E5.2.5.8"),sQuery(id+"F0.wireOp",EDGE,"E5.3.0.5"),sQuery(id+"F0.wireOp",EDGE,"E5.3.0.6"),sQuery(id+"F0.wireOp",EDGE,"E5.3.0.7"),sQuery(id+"F0.wireOp",EDGE,"E5.3.0.8"),sQuery(id+"F0.wireOp",EDGE,"E5.3.1.5"),sQuery(id+"F0.wireOp",EDGE,"E5.3.1.6"),sQuery(id+"F0.wireOp",EDGE,"E5.3.1.7"),sQuery(id+"F0.wireOp",EDGE,"E5.3.1.8"),sQuery(id+"F0.wireOp",EDGE,"E5.3.2.5"),sQuery(id+"F0.wireOp",EDGE,"E5.3.2.6"),sQuery(id+"F0.wireOp",EDGE,"E5.3.2.7"),sQuery(id+"F0.wireOp",EDGE,"E5.3.2.8"),sQuery(id+"F0.wireOp",EDGE,"E5.3.3.5"),sQuery(id+"F0.wireOp",EDGE,"E5.3.3.6"),sQuery(id+"F0.wireOp",EDGE,"E5.3.3.7"),sQuery(id+"F0.wireOp",EDGE,"E5.3.3.8"),sQuery(id+"F0.wireOp",EDGE,"E5.3.4.5"),sQuery(id+"F0.wireOp",EDGE,"E5.3.4.6"),sQuery(id+"F0.wireOp",EDGE,"E5.3.4.7"),sQuery(id+"F0.wireOp",EDGE,"E5.3.4.8"),sQuery(id+"F0.wireOp",EDGE,"E5.3.5.5"),sQuery(id+"F0.wireOp",EDGE,"E5.3.5.6"),sQuery(id+"F0.wireOp",EDGE,"E5.3.5.7"),sQuery(id+"F0.wireOp",EDGE,"E5.3.5.8"),sQuery(id+"F0.wireOp",EDGE,"E5.4.0.5"),sQuery(id+"F0.wireOp",EDGE,"E5.4.0.6"),sQuery(id+"F0.wireOp",EDGE,"E5.4.0.7"),sQuery(id+"F0.wireOp",EDGE,"E5.4.0.8"),sQuery(id+"F0.wireOp",EDGE,"E5.4.1.5"),sQuery(id+"F0.wireOp",EDGE,"E5.4.1.6"),sQuery(id+"F0.wireOp",EDGE,"E5.4.1.7"),sQuery(id+"F0.wireOp",EDGE,"E5.4.1.8"),sQuery(id+"F0.wireOp",EDGE,"E5.4.2.5"),sQuery(id+"F0.wireOp",EDGE,"E5.4.2.6"),sQuery(id+"F0.wireOp",EDGE,"E5.4.2.7"),sQuery(id+"F0.wireOp",EDGE,"E5.4.2.8"),sQuery(id+"F0.wireOp",EDGE,"E5.4.3.5"),sQuery(id+"F0.wireOp",EDGE,"E5.4.3.6"),sQuery(id+"F0.wireOp",EDGE,"E5.4.3.7"),sQuery(id+"F0.wireOp",EDGE,"E5.4.3.8"),sQuery(id+"F0.wireOp",EDGE,"E5.4.4.5"),sQuery(id+"F0.wireOp",EDGE,"E5.4.4.6"),sQuery(id+"F0.wireOp",EDGE,"E5.4.4.7"),sQuery(id+"F0.wireOp",EDGE,"E5.4.4.8"),sQuery(id+"F0.wireOp",EDGE,"E5.4.5.5"),sQuery(id+"F0.wireOp",EDGE,"E5.4.5.6"),sQuery(id+"F0.wireOp",EDGE,"E5.4.5.7"),sQuery(id+"F0.wireOp",EDGE,"E5.4.5.8"),sQuery(id+"F0.wireOp",EDGE,"E5.5.0.5"),sQuery(id+"F0.wireOp",EDGE,"E5.5.0.6"),sQuery(id+"F0.wireOp",EDGE,"E5.5.0.7"),sQuery(id+"F0.wireOp",EDGE,"E5.5.0.8"),sQuery(id+"F0.wireOp",EDGE,"E5.5.1.5"),sQuery(id+"F0.wireOp",EDGE,"E5.5.1.6"),sQuery(id+"F0.wireOp",EDGE,"E5.5.1.7"),sQuery(id+"F0.wireOp",EDGE,"E5.5.1.8"),sQuery(id+"F0.wireOp",EDGE,"E5.5.2.5"),sQuery(id+"F0.wireOp",EDGE,"E5.5.2.6"),sQuery(id+"F0.wireOp",EDGE,"E5.5.2.7"),sQuery(id+"F0.wireOp",EDGE,"E5.5.2.8"),sQuery(id+"F0.wireOp",EDGE,"E5.5.3.5"),sQuery(id+"F0.wireOp",EDGE,"E5.5.3.6"),sQuery(id+"F0.wireOp",EDGE,"E5.5.3.7"),sQuery(id+"F0.wireOp",EDGE,"E5.5.3.8"),sQuery(id+"F0.wireOp",EDGE,"E5.5.4.5"),sQuery(id+"F0.wireOp",EDGE,"E5.5.4.6"),sQuery(id+"F0.wireOp",EDGE,"E5.5.4.7"),sQuery(id+"F0.wireOp",EDGE,"E5.5.4.8"),sQuery(id+"F0.wireOp",EDGE,"E5.5.5.5"),sQuery(id+"F0.wireOp",EDGE,"E5.5.5.6"),sQuery(id+"F0.wireOp",EDGE,"E5.5.5.7"),sQuery(id+"F0.wireOp",EDGE,"E5.5.5.8"),sQuery(id+"F0.wireOp",EDGE,"E6.13.6.0"),sQuery(id+"F0.wireOp",EDGE,"E6.15.6.0"),sQuery(id+"F0.wireOp",EDGE,"E6.17.6.0"),sQuery(id+"F0.wireOp",EDGE,"E6.19.6.0"),sQuery(id+"F0.wireOp",EDGE,"E6.13.6.1"),sQuery(id+"F0.wireOp",EDGE,"E6.15.6.1"),sQuery(id+"F0.wireOp",EDGE,"E6.17.6.1"),sQuery(id+"F0.wireOp",EDGE,"E6.19.6.1"),sQuery(id+"F0.wireOp",EDGE,"E6.13.6.2"),sQuery(id+"F0.wireOp",EDGE,"E6.15.6.2"),sQuery(id+"F0.wireOp",EDGE,"E6.17.6.2"),sQuery(id+"F0.wireOp",EDGE,"E6.19.6.2"),sQuery(id+"F0.wireOp",EDGE,"E6.13.6.3"),sQuery(id+"F0.wireOp",EDGE,"E6.15.6.3"),sQuery(id+"F0.wireOp",EDGE,"E6.17.6.3"),sQuery(id+"F0.wireOp",EDGE,"E6.19.6.3"),sQuery(id+"F0.wireOp",EDGE,"E6.13.6.4"),sQuery(id+"F0.wireOp",EDGE,"E6.15.6.4"),sQuery(id+"F0.wireOp",EDGE,"E6.17.6.4"),sQuery(id+"F0.wireOp",EDGE,"E6.19.6.4"),sQuery(id+"F0.wireOp",EDGE,"E6.13.6.5"),sQuery(id+"F0.wireOp",EDGE,"E6.15.6.5"),sQuery(id+"F0.wireOp",EDGE,"E6.17.6.5"),sQuery(id+"F0.wireOp",EDGE,"E6.19.6.5"),sQuery(id+"F0.wireOp",EDGE,"E7.13.7.0"),sQuery(id+"F0.wireOp",EDGE,"E7.15.7.0"),sQuery(id+"F0.wireOp",EDGE,"E7.17.7.0"),sQuery(id+"F0.wireOp",EDGE,"E7.19.7.0"),sQuery(id+"F0.wireOp",EDGE,"E7.13.7.1"),sQuery(id+"F0.wireOp",EDGE,"E7.15.7.1"),sQuery(id+"F0.wireOp",EDGE,"E7.17.7.1"),sQuery(id+"F0.wireOp",EDGE,"E7.19.7.1"),sQuery(id+"F0.wireOp",EDGE,"E7.13.7.2"),sQuery(id+"F0.wireOp",EDGE,"E7.15.7.2"),sQuery(id+"F0.wireOp",EDGE,"E7.17.7.2"),sQuery(id+"F0.wireOp",EDGE,"E7.19.7.2"),sQuery(id+"F0.wireOp",EDGE,"E7.13.7.3"),sQuery(id+"F0.wireOp",EDGE,"E7.15.7.3"),sQuery(id+"F0.wireOp",EDGE,"E7.17.7.3"),sQuery(id+"F0.wireOp",EDGE,"E7.19.7.3"),sQuery(id+"F0.wireOp",EDGE,"E7.13.7.4"),sQuery(id+"F0.wireOp",EDGE,"E7.15.7.4"),sQuery(id+"F0.wireOp",EDGE,"E7.17.7.4"),sQuery(id+"F0.wireOp",EDGE,"E7.19.7.4"),sQuery(id+"F0.wireOp",EDGE,"E7.13.7.5"),sQuery(id+"F0.wireOp",EDGE,"E7.15.7.5"),sQuery(id+"F0.wireOp",EDGE,"E7.17.7.5"),sQuery(id+"F0.wireOp",EDGE,"E7.19.7.5"),sQuery(id+"F0.wireOp",EDGE,"E8.13.0.6"),sQuery(id+"F0.wireOp",EDGE,"E8.15.0.6"),sQuery(id+"F0.wireOp",EDGE,"E8.17.0.6"),sQuery(id+"F0.wireOp",EDGE,"E8.19.0.6"),sQuery(id+"F0.wireOp",EDGE,"E8.13.1.6"),sQuery(id+"F0.wireOp",EDGE,"E8.15.1.6"),sQuery(id+"F0.wireOp",EDGE,"E8.17.1.6"),sQuery(id+"F0.wireOp",EDGE,"E8.19.1.6"),sQuery(id+"F0.wireOp",EDGE,"E8.13.2.6"),sQuery(id+"F0.wireOp",EDGE,"E8.15.2.6"),sQuery(id+"F0.wireOp",EDGE,"E8.17.2.6"),sQuery(id+"F0.wireOp",EDGE,"E8.19.2.6"),sQuery(id+"F0.wireOp",EDGE,"E8.13.3.6"),sQuery(id+"F0.wireOp",EDGE,"E8.15.3.6"),sQuery(id+"F0.wireOp",EDGE,"E8.17.3.6"),sQuery(id+"F0.wireOp",EDGE,"E8.19.3.6"),sQuery(id+"F0.wireOp",EDGE,"E8.13.4.6"),sQuery(id+"F0.wireOp",EDGE,"E8.15.4.6"),sQuery(id+"F0.wireOp",EDGE,"E8.17.4.6"),sQuery(id+"F0.wireOp",EDGE,"E8.19.4.6"),sQuery(id+"F0.wireOp",EDGE,"E8.13.5.6"),sQuery(id+"F0.wireOp",EDGE,"E8.15.5.6"),sQuery(id+"F0.wireOp",EDGE,"E8.17.5.6"),sQuery(id+"F0.wireOp",EDGE,"E8.19.5.6"),sQuery(id+"F0.wireOp",EDGE,"E8.13.6.6"),sQuery(id+"F0.wireOp",EDGE,"E8.15.6.6"),sQuery(id+"F0.wireOp",EDGE,"E8.17.6.6"),sQuery(id+"F0.wireOp",EDGE,"E8.19.6.6"),sQuery(id+"F0.wireOp",EDGE,"E8.13.7.6"),sQuery(id+"F0.wireOp",EDGE,"E8.15.7.6"),sQuery(id+"F0.wireOp",EDGE,"E8.17.7.6"),sQuery(id+"F0.wireOp",EDGE,"E8.19.7.6"),sQuery(id+"F0.wireOp",EDGE,"E9.13.0.7"),sQuery(id+"F0.wireOp",EDGE,"E9.15.0.7"),sQuery(id+"F0.wireOp",EDGE,"E9.17.0.7"),sQuery(id+"F0.wireOp",EDGE,"E9.19.0.7"),sQuery(id+"F0.wireOp",EDGE,"E9.13.1.7"),sQuery(id+"F0.wireOp",EDGE,"E9.15.1.7"),sQuery(id+"F0.wireOp",EDGE,"E9.17.1.7"),sQuery(id+"F0.wireOp",EDGE,"E9.19.1.7"),sQuery(id+"F0.wireOp",EDGE,"E9.13.2.7"),sQuery(id+"F0.wireOp",EDGE,"E9.15.2.7"),sQuery(id+"F0.wireOp",EDGE,"E9.17.2.7"),sQuery(id+"F0.wireOp",EDGE,"E9.19.2.7"),sQuery(id+"F0.wireOp",EDGE,"E9.13.3.7"),sQuery(id+"F0.wireOp",EDGE,"E9.15.3.7"),sQuery(id+"F0.wireOp",EDGE,"E9.17.3.7"),sQuery(id+"F0.wireOp",EDGE,"E9.19.3.7"),sQuery(id+"F0.wireOp",EDGE,"E9.13.4.7"),sQuery(id+"F0.wireOp",EDGE,"E9.15.4.7"),sQuery(id+"F0.wireOp",EDGE,"E9.17.4.7"),sQuery(id+"F0.wireOp",EDGE,"E9.19.4.7"),sQuery(id+"F0.wireOp",EDGE,"E9.13.5.7"),sQuery(id+"F0.wireOp",EDGE,"E9.15.5.7"),sQuery(id+"F0.wireOp",EDGE,"E9.17.5.7"),sQuery(id+"F0.wireOp",EDGE,"E9.19.5.7"),sQuery(id+"F0.wireOp",EDGE,"E9.13.6.7"),sQuery(id+"F0.wireOp",EDGE,"E9.15.6.7"),sQuery(id+"F0.wireOp",EDGE,"E9.17.6.7"),sQuery(id+"F0.wireOp",EDGE,"E9.19.6.7"),sQuery(id+"F0.wireOp",EDGE,"E9.13.7.7"),sQuery(id+"F0.wireOp",EDGE,"E9.15.7.7"),sQuery(id+"F0.wireOp",EDGE,"E9.17.7.7"),sQuery(id+"F0.wireOp",EDGE,"E9.19.7.7"),sQuery(id+"F0.wireOp",EDGE,"E10.bottom"),sQuery(id+"F0.wireOp",EDGE,"E10.top"),sQuery(id+"F0.wireOp",EDGE,"E10.left"),sQuery(id+"F0.wireOp",EDGE,"E10.right")])],"isStart":false});
            var sketch = newSketch(context, id + "F2", { "sketchPlane" : qUnion([Q0])});
            skLineSegment(sketch, "E11.bottom", {"start": v(-7.5, -7.5) * mm, "end": v(77.5, -7.5) * mm});
            skLineSegment(sketch, "E11.top", {"start": v(-7.5, 77.5) * mm, "end": v(77.5, 77.5) * mm});
            skLineSegment(sketch, "E11.left", {"start": v(-7.5, -7.5) * mm, "end": v(-7.5, 77.5) * mm});
            skLineSegment(sketch, "E11.right", {"start": v(77.5, -7.5) * mm, "end": v(77.5, 77.5) * mm});
            skSolve(sketch);
        }
        {
            var Q0;
            Q0 = qSketchRegion(id + "F2", true);
            extrude(context, id + "F3", {"entities" : qUnion([Q0]), "operationType" : NewBodyOperationType.ADD, "oppositeDirection" : true, "depth" : .8 * mm});
        }
        {
            var Q0;
            Q0=makeQuery(id+"F3.boolean.opBoolean","MERGE",FACE,{"derivedFrom":[makeQuery(id+"F1.opExtrude","CAP_FACE",FACE,{"disambiguationData":[OSD([sQuery(id+"F0.wireOp",EDGE,"E1"),sQuery(id+"F0.wireOp",EDGE,"E2"),sQuery(id+"F0.wireOp",EDGE,"E3"),sQuery(id+"F0.wireOp",EDGE,"E4"),sQuery(id+"F0.wireOp",EDGE,"E5.0.1.5"),sQuery(id+"F0.wireOp",EDGE,"E5.0.1.6"),sQuery(id+"F0.wireOp",EDGE,"E5.0.1.7"),sQuery(id+"F0.wireOp",EDGE,"E5.0.1.8"),sQuery(id+"F0.wireOp",EDGE,"E5.0.2.5"),sQuery(id+"F0.wireOp",EDGE,"E5.0.2.6"),sQuery(id+"F0.wireOp",EDGE,"E5.0.2.7"),sQuery(id+"F0.wireOp",EDGE,"E5.0.2.8"),sQuery(id+"F0.wireOp",EDGE,"E5.0.3.5"),sQuery(id+"F0.wireOp",EDGE,"E5.0.3.6"),sQuery(id+"F0.wireOp",EDGE,"E5.0.3.7"),sQuery(id+"F0.wireOp",EDGE,"E5.0.3.8"),sQuery(id+"F0.wireOp",EDGE,"E5.0.4.5"),sQuery(id+"F0.wireOp",EDGE,"E5.0.4.6"),sQuery(id+"F0.wireOp",EDGE,"E5.0.4.7"),sQuery(id+"F0.wireOp",EDGE,"E5.0.4.8"),sQuery(id+"F0.wireOp",EDGE,"E5.0.5.5"),sQuery(id+"F0.wireOp",EDGE,"E5.0.5.6"),sQuery(id+"F0.wireOp",EDGE,"E5.0.5.7"),sQuery(id+"F0.wireOp",EDGE,"E5.0.5.8"),sQuery(id+"F0.wireOp",EDGE,"E5.1.0.5"),sQuery(id+"F0.wireOp",EDGE,"E5.1.0.6"),sQuery(id+"F0.wireOp",EDGE,"E5.1.0.7"),sQuery(id+"F0.wireOp",EDGE,"E5.1.0.8"),sQuery(id+"F0.wireOp",EDGE,"E5.1.1.5"),sQuery(id+"F0.wireOp",EDGE,"E5.1.1.6"),sQuery(id+"F0.wireOp",EDGE,"E5.1.1.7"),sQuery(id+"F0.wireOp",EDGE,"E5.1.1.8"),sQuery(id+"F0.wireOp",EDGE,"E5.1.2.5"),sQuery(id+"F0.wireOp",EDGE,"E5.1.2.6"),sQuery(id+"F0.wireOp",EDGE,"E5.1.2.7"),sQuery(id+"F0.wireOp",EDGE,"E5.1.2.8"),sQuery(id+"F0.wireOp",EDGE,"E5.1.3.5"),sQuery(id+"F0.wireOp",EDGE,"E5.1.3.6"),sQuery(id+"F0.wireOp",EDGE,"E5.1.3.7"),sQuery(id+"F0.wireOp",EDGE,"E5.1.3.8"),sQuery(id+"F0.wireOp",EDGE,"E5.1.4.5"),sQuery(id+"F0.wireOp",EDGE,"E5.1.4.6"),sQuery(id+"F0.wireOp",EDGE,"E5.1.4.7"),sQuery(id+"F0.wireOp",EDGE,"E5.1.4.8"),sQuery(id+"F0.wireOp",EDGE,"E5.1.5.5"),sQuery(id+"F0.wireOp",EDGE,"E5.1.5.6"),sQuery(id+"F0.wireOp",EDGE,"E5.1.5.7"),sQuery(id+"F0.wireOp",EDGE,"E5.1.5.8"),sQuery(id+"F0.wireOp",EDGE,"E5.2.0.5"),sQuery(id+"F0.wireOp",EDGE,"E5.2.0.6"),sQuery(id+"F0.wireOp",EDGE,"E5.2.0.7"),sQuery(id+"F0.wireOp",EDGE,"E5.2.0.8"),sQuery(id+"F0.wireOp",EDGE,"E5.2.1.5"),sQuery(id+"F0.wireOp",EDGE,"E5.2.1.6"),sQuery(id+"F0.wireOp",EDGE,"E5.2.1.7"),sQuery(id+"F0.wireOp",EDGE,"E5.2.1.8"),sQuery(id+"F0.wireOp",EDGE,"E5.2.2.5"),sQuery(id+"F0.wireOp",EDGE,"E5.2.2.6"),sQuery(id+"F0.wireOp",EDGE,"E5.2.2.7"),sQuery(id+"F0.wireOp",EDGE,"E5.2.2.8"),sQuery(id+"F0.wireOp",EDGE,"E5.2.3.5"),sQuery(id+"F0.wireOp",EDGE,"E5.2.3.6"),sQuery(id+"F0.wireOp",EDGE,"E5.2.3.7"),sQuery(id+"F0.wireOp",EDGE,"E5.2.3.8"),sQuery(id+"F0.wireOp",EDGE,"E5.2.4.5"),sQuery(id+"F0.wireOp",EDGE,"E5.2.4.6"),sQuery(id+"F0.wireOp",EDGE,"E5.2.4.7"),sQuery(id+"F0.wireOp",EDGE,"E5.2.4.8"),sQuery(id+"F0.wireOp",EDGE,"E5.2.5.5"),sQuery(id+"F0.wireOp",EDGE,"E5.2.5.6"),sQuery(id+"F0.wireOp",EDGE,"E5.2.5.7"),sQuery(id+"F0.wireOp",EDGE,"E5.2.5.8"),sQuery(id+"F0.wireOp",EDGE,"E5.3.0.5"),sQuery(id+"F0.wireOp",EDGE,"E5.3.0.6"),sQuery(id+"F0.wireOp",EDGE,"E5.3.0.7"),sQuery(id+"F0.wireOp",EDGE,"E5.3.0.8"),sQuery(id+"F0.wireOp",EDGE,"E5.3.1.5"),sQuery(id+"F0.wireOp",EDGE,"E5.3.1.6"),sQuery(id+"F0.wireOp",EDGE,"E5.3.1.7"),sQuery(id+"F0.wireOp",EDGE,"E5.3.1.8"),sQuery(id+"F0.wireOp",EDGE,"E5.3.2.5"),sQuery(id+"F0.wireOp",EDGE,"E5.3.2.6"),sQuery(id+"F0.wireOp",EDGE,"E5.3.2.7"),sQuery(id+"F0.wireOp",EDGE,"E5.3.2.8"),sQuery(id+"F0.wireOp",EDGE,"E5.3.3.5"),sQuery(id+"F0.wireOp",EDGE,"E5.3.3.6"),sQuery(id+"F0.wireOp",EDGE,"E5.3.3.7"),sQuery(id+"F0.wireOp",EDGE,"E5.3.3.8"),sQuery(id+"F0.wireOp",EDGE,"E5.3.4.5"),sQuery(id+"F0.wireOp",EDGE,"E5.3.4.6"),sQuery(id+"F0.wireOp",EDGE,"E5.3.4.7"),sQuery(id+"F0.wireOp",EDGE,"E5.3.4.8"),sQuery(id+"F0.wireOp",EDGE,"E5.3.5.5"),sQuery(id+"F0.wireOp",EDGE,"E5.3.5.6"),sQuery(id+"F0.wireOp",EDGE,"E5.3.5.7"),sQuery(id+"F0.wireOp",EDGE,"E5.3.5.8"),sQuery(id+"F0.wireOp",EDGE,"E5.4.0.5"),sQuery(id+"F0.wireOp",EDGE,"E5.4.0.6"),sQuery(id+"F0.wireOp",EDGE,"E5.4.0.7"),sQuery(id+"F0.wireOp",EDGE,"E5.4.0.8"),sQuery(id+"F0.wireOp",EDGE,"E5.4.1.5"),sQuery(id+"F0.wireOp",EDGE,"E5.4.1.6"),sQuery(id+"F0.wireOp",EDGE,"E5.4.1.7"),sQuery(id+"F0.wireOp",EDGE,"E5.4.1.8"),sQuery(id+"F0.wireOp",EDGE,"E5.4.2.5"),sQuery(id+"F0.wireOp",EDGE,"E5.4.2.6"),sQuery(id+"F0.wireOp",EDGE,"E5.4.2.7"),sQuery(id+"F0.wireOp",EDGE,"E5.4.2.8"),sQuery(id+"F0.wireOp",EDGE,"E5.4.3.5"),sQuery(id+"F0.wireOp",EDGE,"E5.4.3.6"),sQuery(id+"F0.wireOp",EDGE,"E5.4.3.7"),sQuery(id+"F0.wireOp",EDGE,"E5.4.3.8"),sQuery(id+"F0.wireOp",EDGE,"E5.4.4.5"),sQuery(id+"F0.wireOp",EDGE,"E5.4.4.6"),sQuery(id+"F0.wireOp",EDGE,"E5.4.4.7"),sQuery(id+"F0.wireOp",EDGE,"E5.4.4.8"),sQuery(id+"F0.wireOp",EDGE,"E5.4.5.5"),sQuery(id+"F0.wireOp",EDGE,"E5.4.5.6"),sQuery(id+"F0.wireOp",EDGE,"E5.4.5.7"),sQuery(id+"F0.wireOp",EDGE,"E5.4.5.8"),sQuery(id+"F0.wireOp",EDGE,"E5.5.0.5"),sQuery(id+"F0.wireOp",EDGE,"E5.5.0.6"),sQuery(id+"F0.wireOp",EDGE,"E5.5.0.7"),sQuery(id+"F0.wireOp",EDGE,"E5.5.0.8"),sQuery(id+"F0.wireOp",EDGE,"E5.5.1.5"),sQuery(id+"F0.wireOp",EDGE,"E5.5.1.6"),sQuery(id+"F0.wireOp",EDGE,"E5.5.1.7"),sQuery(id+"F0.wireOp",EDGE,"E5.5.1.8"),sQuery(id+"F0.wireOp",EDGE,"E5.5.2.5"),sQuery(id+"F0.wireOp",EDGE,"E5.5.2.6"),sQuery(id+"F0.wireOp",EDGE,"E5.5.2.7"),sQuery(id+"F0.wireOp",EDGE,"E5.5.2.8"),sQuery(id+"F0.wireOp",EDGE,"E5.5.3.5"),sQuery(id+"F0.wireOp",EDGE,"E5.5.3.6"),sQuery(id+"F0.wireOp",EDGE,"E5.5.3.7"),sQuery(id+"F0.wireOp",EDGE,"E5.5.3.8"),sQuery(id+"F0.wireOp",EDGE,"E5.5.4.5"),sQuery(id+"F0.wireOp",EDGE,"E5.5.4.6"),sQuery(id+"F0.wireOp",EDGE,"E5.5.4.7"),sQuery(id+"F0.wireOp",EDGE,"E5.5.4.8"),sQuery(id+"F0.wireOp",EDGE,"E5.5.5.5"),sQuery(id+"F0.wireOp",EDGE,"E5.5.5.6"),sQuery(id+"F0.wireOp",EDGE,"E5.5.5.7"),sQuery(id+"F0.wireOp",EDGE,"E5.5.5.8"),sQuery(id+"F0.wireOp",EDGE,"E6.13.6.0"),sQuery(id+"F0.wireOp",EDGE,"E6.15.6.0"),sQuery(id+"F0.wireOp",EDGE,"E6.17.6.0"),sQuery(id+"F0.wireOp",EDGE,"E6.19.6.0"),sQuery(id+"F0.wireOp",EDGE,"E6.13.6.1"),sQuery(id+"F0.wireOp",EDGE,"E6.15.6.1"),sQuery(id+"F0.wireOp",EDGE,"E6.17.6.1"),sQuery(id+"F0.wireOp",EDGE,"E6.19.6.1"),sQuery(id+"F0.wireOp",EDGE,"E6.13.6.2"),sQuery(id+"F0.wireOp",EDGE,"E6.15.6.2"),sQuery(id+"F0.wireOp",EDGE,"E6.17.6.2"),sQuery(id+"F0.wireOp",EDGE,"E6.19.6.2"),sQuery(id+"F0.wireOp",EDGE,"E6.13.6.3"),sQuery(id+"F0.wireOp",EDGE,"E6.15.6.3"),sQuery(id+"F0.wireOp",EDGE,"E6.17.6.3"),sQuery(id+"F0.wireOp",EDGE,"E6.19.6.3"),sQuery(id+"F0.wireOp",EDGE,"E6.13.6.4"),sQuery(id+"F0.wireOp",EDGE,"E6.15.6.4"),sQuery(id+"F0.wireOp",EDGE,"E6.17.6.4"),sQuery(id+"F0.wireOp",EDGE,"E6.19.6.4"),sQuery(id+"F0.wireOp",EDGE,"E6.13.6.5"),sQuery(id+"F0.wireOp",EDGE,"E6.15.6.5"),sQuery(id+"F0.wireOp",EDGE,"E6.17.6.5"),sQuery(id+"F0.wireOp",EDGE,"E6.19.6.5"),sQuery(id+"F0.wireOp",EDGE,"E7.13.7.0"),sQuery(id+"F0.wireOp",EDGE,"E7.15.7.0"),sQuery(id+"F0.wireOp",EDGE,"E7.17.7.0"),sQuery(id+"F0.wireOp",EDGE,"E7.19.7.0"),sQuery(id+"F0.wireOp",EDGE,"E7.13.7.1"),sQuery(id+"F0.wireOp",EDGE,"E7.15.7.1"),sQuery(id+"F0.wireOp",EDGE,"E7.17.7.1"),sQuery(id+"F0.wireOp",EDGE,"E7.19.7.1"),sQuery(id+"F0.wireOp",EDGE,"E7.13.7.2"),sQuery(id+"F0.wireOp",EDGE,"E7.15.7.2"),sQuery(id+"F0.wireOp",EDGE,"E7.17.7.2"),sQuery(id+"F0.wireOp",EDGE,"E7.19.7.2"),sQuery(id+"F0.wireOp",EDGE,"E7.13.7.3"),sQuery(id+"F0.wireOp",EDGE,"E7.15.7.3"),sQuery(id+"F0.wireOp",EDGE,"E7.17.7.3"),sQuery(id+"F0.wireOp",EDGE,"E7.19.7.3"),sQuery(id+"F0.wireOp",EDGE,"E7.13.7.4"),sQuery(id+"F0.wireOp",EDGE,"E7.15.7.4"),sQuery(id+"F0.wireOp",EDGE,"E7.17.7.4"),sQuery(id+"F0.wireOp",EDGE,"E7.19.7.4"),sQuery(id+"F0.wireOp",EDGE,"E7.13.7.5"),sQuery(id+"F0.wireOp",EDGE,"E7.15.7.5"),sQuery(id+"F0.wireOp",EDGE,"E7.17.7.5"),sQuery(id+"F0.wireOp",EDGE,"E7.19.7.5"),sQuery(id+"F0.wireOp",EDGE,"E8.13.0.6"),sQuery(id+"F0.wireOp",EDGE,"E8.15.0.6"),sQuery(id+"F0.wireOp",EDGE,"E8.17.0.6"),sQuery(id+"F0.wireOp",EDGE,"E8.19.0.6"),sQuery(id+"F0.wireOp",EDGE,"E8.13.1.6"),sQuery(id+"F0.wireOp",EDGE,"E8.15.1.6"),sQuery(id+"F0.wireOp",EDGE,"E8.17.1.6"),sQuery(id+"F0.wireOp",EDGE,"E8.19.1.6"),sQuery(id+"F0.wireOp",EDGE,"E8.13.2.6"),sQuery(id+"F0.wireOp",EDGE,"E8.15.2.6"),sQuery(id+"F0.wireOp",EDGE,"E8.17.2.6"),sQuery(id+"F0.wireOp",EDGE,"E8.19.2.6"),sQuery(id+"F0.wireOp",EDGE,"E8.13.3.6"),sQuery(id+"F0.wireOp",EDGE,"E8.15.3.6"),sQuery(id+"F0.wireOp",EDGE,"E8.17.3.6"),sQuery(id+"F0.wireOp",EDGE,"E8.19.3.6"),sQuery(id+"F0.wireOp",EDGE,"E8.13.4.6"),sQuery(id+"F0.wireOp",EDGE,"E8.15.4.6"),sQuery(id+"F0.wireOp",EDGE,"E8.17.4.6"),sQuery(id+"F0.wireOp",EDGE,"E8.19.4.6"),sQuery(id+"F0.wireOp",EDGE,"E8.13.5.6"),sQuery(id+"F0.wireOp",EDGE,"E8.15.5.6"),sQuery(id+"F0.wireOp",EDGE,"E8.17.5.6"),sQuery(id+"F0.wireOp",EDGE,"E8.19.5.6"),sQuery(id+"F0.wireOp",EDGE,"E8.13.6.6"),sQuery(id+"F0.wireOp",EDGE,"E8.15.6.6"),sQuery(id+"F0.wireOp",EDGE,"E8.17.6.6"),sQuery(id+"F0.wireOp",EDGE,"E8.19.6.6"),sQuery(id+"F0.wireOp",EDGE,"E8.13.7.6"),sQuery(id+"F0.wireOp",EDGE,"E8.15.7.6"),sQuery(id+"F0.wireOp",EDGE,"E8.17.7.6"),sQuery(id+"F0.wireOp",EDGE,"E8.19.7.6"),sQuery(id+"F0.wireOp",EDGE,"E9.13.0.7"),sQuery(id+"F0.wireOp",EDGE,"E9.15.0.7"),sQuery(id+"F0.wireOp",EDGE,"E9.17.0.7"),sQuery(id+"F0.wireOp",EDGE,"E9.19.0.7"),sQuery(id+"F0.wireOp",EDGE,"E9.13.1.7"),sQuery(id+"F0.wireOp",EDGE,"E9.15.1.7"),sQuery(id+"F0.wireOp",EDGE,"E9.17.1.7"),sQuery(id+"F0.wireOp",EDGE,"E9.19.1.7"),sQuery(id+"F0.wireOp",EDGE,"E9.13.2.7"),sQuery(id+"F0.wireOp",EDGE,"E9.15.2.7"),sQuery(id+"F0.wireOp",EDGE,"E9.17.2.7"),sQuery(id+"F0.wireOp",EDGE,"E9.19.2.7"),sQuery(id+"F0.wireOp",EDGE,"E9.13.3.7"),sQuery(id+"F0.wireOp",EDGE,"E9.15.3.7"),sQuery(id+"F0.wireOp",EDGE,"E9.17.3.7"),sQuery(id+"F0.wireOp",EDGE,"E9.19.3.7"),sQuery(id+"F0.wireOp",EDGE,"E9.13.4.7"),sQuery(id+"F0.wireOp",EDGE,"E9.15.4.7"),sQuery(id+"F0.wireOp",EDGE,"E9.17.4.7"),sQuery(id+"F0.wireOp",EDGE,"E9.19.4.7"),sQuery(id+"F0.wireOp",EDGE,"E9.13.5.7"),sQuery(id+"F0.wireOp",EDGE,"E9.15.5.7"),sQuery(id+"F0.wireOp",EDGE,"E9.17.5.7"),sQuery(id+"F0.wireOp",EDGE,"E9.19.5.7"),sQuery(id+"F0.wireOp",EDGE,"E9.13.6.7"),sQuery(id+"F0.wireOp",EDGE,"E9.15.6.7"),sQuery(id+"F0.wireOp",EDGE,"E9.17.6.7"),sQuery(id+"F0.wireOp",EDGE,"E9.19.6.7"),sQuery(id+"F0.wireOp",EDGE,"E9.13.7.7"),sQuery(id+"F0.wireOp",EDGE,"E9.15.7.7"),sQuery(id+"F0.wireOp",EDGE,"E9.17.7.7"),sQuery(id+"F0.wireOp",EDGE,"E9.19.7.7"),sQuery(id+"F0.wireOp",EDGE,"E10.bottom"),sQuery(id+"F0.wireOp",EDGE,"E10.top"),sQuery(id+"F0.wireOp",EDGE,"E10.left"),sQuery(id+"F0.wireOp",EDGE,"E10.right")])],"isStart":false}),makeQuery(id+"F3.opExtrude","CAP_FACE",FACE,{"disambiguationData":[OSD([sQuery(id+"F2.wireOp",EDGE,"E11.bottom"),sQuery(id+"F2.wireOp",EDGE,"E11.top"),sQuery(id+"F2.wireOp",EDGE,"E11.left"),sQuery(id+"F2.wireOp",EDGE,"E11.right")])],"isStart":true})]});
            var sketch = newSketch(context, id + "F4", { "sketchPlane" : qUnion([Q0])});
            skLineSegment(sketch, "E12.bottom", {"start": v(5.75, -0.75) * mm, "end": v(-0.75, -0.75) * mm, "construction": true});
            skLineSegment(sketch, "E12.top", {"start": v(5.75, 5.75) * mm, "end": v(-0.75, 5.75) * mm, "construction": true});
            skLineSegment(sketch, "E12.left", {"start": v(5.75, -0.75) * mm, "end": v(5.75, 5.75) * mm, "construction": true});
            skLineSegment(sketch, "E12.right", {"start": v(-0.75, -0.75) * mm, "end": v(-0.75, 5.75) * mm, "construction": true});
            skPoint(sketch, "E12.middle", {"position": v(2.5, 2.5) * mm});
            skCircle(sketch, "E13", {"center": v(-0.75, 5.75) * mm, "radius": 1.3 * mm});
            skCircle(sketch, "E14", {"center": v(5.75, 5.75) * mm, "radius": 1.3 * mm});
            skCircle(sketch, "E15", {"center": v(5.75, -0.75) * mm, "radius": 1.3 * mm});
            skCircle(sketch, "E16", {"center": v(-0.75, -0.75) * mm, "radius": 1.3 * mm});
            skPoint(sketch, "E17.0.1.0", {"position": v(2.5, 15.5) * mm});
            skLineSegment(sketch, "E17.0.1.1", {"start": v(-0.75, 12.25) * mm, "end": v(-0.75, 18.75) * mm, "construction": true});
            skLineSegment(sketch, "E17.0.1.2", {"start": v(5.75, 12.25) * mm, "end": v(5.75, 18.75) * mm, "construction": true});
            skLineSegment(sketch, "E17.0.1.3", {"start": v(5.75, 12.25) * mm, "end": v(-0.75, 12.25) * mm, "construction": true});
            skLineSegment(sketch, "E17.0.1.4", {"start": v(5.75, 18.75) * mm, "end": v(-0.75, 18.75) * mm, "construction": true});
            skCircle(sketch, "E17.0.1.5", {"center": v(-0.75, 12.25) * mm, "radius": 1.3 * mm});
            skCircle(sketch, "E17.0.1.6", {"center": v(5.75, 12.25) * mm, "radius": 1.3 * mm});
            skCircle(sketch, "E17.0.1.7", {"center": v(5.75, 18.75) * mm, "radius": 1.3 * mm});
            skCircle(sketch, "E17.0.1.8", {"center": v(-0.75, 18.75) * mm, "radius": 1.3 * mm});
            skPoint(sketch, "E17.0.2.0", {"position": v(2.5, 28.5) * mm});
            skLineSegment(sketch, "E17.0.2.1", {"start": v(-0.75, 25.25) * mm, "end": v(-0.75, 31.75) * mm, "construction": true});
            skLineSegment(sketch, "E17.0.2.2", {"start": v(5.75, 25.25) * mm, "end": v(5.75, 31.75) * mm, "construction": true});
            skLineSegment(sketch, "E17.0.2.3", {"start": v(5.75, 25.25) * mm, "end": v(-0.75, 25.25) * mm, "construction": true});
            skLineSegment(sketch, "E17.0.2.4", {"start": v(5.75, 31.75) * mm, "end": v(-0.75, 31.75) * mm, "construction": true});
            skCircle(sketch, "E17.0.2.5", {"center": v(-0.75, 25.25) * mm, "radius": 1.3 * mm});
            skCircle(sketch, "E17.0.2.6", {"center": v(5.75, 25.25) * mm, "radius": 1.3 * mm});
            skCircle(sketch, "E17.0.2.7", {"center": v(5.75, 31.75) * mm, "radius": 1.3 * mm});
            skCircle(sketch, "E17.0.2.8", {"center": v(-0.75, 31.75) * mm, "radius": 1.3 * mm});
            skPoint(sketch, "E17.0.3.0", {"position": v(2.5, 41.5) * mm});
            skLineSegment(sketch, "E17.0.3.1", {"start": v(-0.75, 38.25) * mm, "end": v(-0.75, 44.75) * mm, "construction": true});
            skLineSegment(sketch, "E17.0.3.2", {"start": v(5.75, 38.25) * mm, "end": v(5.75, 44.75) * mm, "construction": true});
            skLineSegment(sketch, "E17.0.3.3", {"start": v(5.75, 38.25) * mm, "end": v(-0.75, 38.25) * mm, "construction": true});
            skLineSegment(sketch, "E17.0.3.4", {"start": v(5.75, 44.75) * mm, "end": v(-0.75, 44.75) * mm, "construction": true});
            skCircle(sketch, "E17.0.3.5", {"center": v(-0.75, 38.25) * mm, "radius": 1.3 * mm});
            skCircle(sketch, "E17.0.3.6", {"center": v(5.75, 38.25) * mm, "radius": 1.3 * mm});
            skCircle(sketch, "E17.0.3.7", {"center": v(5.75, 44.75) * mm, "radius": 1.3 * mm});
            skCircle(sketch, "E17.0.3.8", {"center": v(-0.75, 44.75) * mm, "radius": 1.3 * mm});
            skPoint(sketch, "E17.0.4.0", {"position": v(2.5, 54.5) * mm});
            skLineSegment(sketch, "E17.0.4.1", {"start": v(-0.75, 51.25) * mm, "end": v(-0.75, 57.75) * mm, "construction": true});
            skLineSegment(sketch, "E17.0.4.2", {"start": v(5.75, 51.25) * mm, "end": v(5.75, 57.75) * mm, "construction": true});
            skLineSegment(sketch, "E17.0.4.3", {"start": v(5.75, 51.25) * mm, "end": v(-0.75, 51.25) * mm, "construction": true});
            skLineSegment(sketch, "E17.0.4.4", {"start": v(5.75, 57.75) * mm, "end": v(-0.75, 57.75) * mm, "construction": true});
            skCircle(sketch, "E17.0.4.5", {"center": v(-0.75, 51.25) * mm, "radius": 1.3 * mm});
            skCircle(sketch, "E17.0.4.6", {"center": v(5.75, 51.25) * mm, "radius": 1.3 * mm});
            skCircle(sketch, "E17.0.4.7", {"center": v(5.75, 57.75) * mm, "radius": 1.3 * mm});
            skCircle(sketch, "E17.0.4.8", {"center": v(-0.75, 57.75) * mm, "radius": 1.3 * mm});
            skPoint(sketch, "E17.0.5.0", {"position": v(2.5, 67.5) * mm});
            skLineSegment(sketch, "E17.0.5.1", {"start": v(-0.75, 64.25) * mm, "end": v(-0.75, 70.75) * mm, "construction": true});
            skLineSegment(sketch, "E17.0.5.2", {"start": v(5.75, 64.25) * mm, "end": v(5.75, 70.75) * mm, "construction": true});
            skLineSegment(sketch, "E17.0.5.3", {"start": v(5.75, 64.25) * mm, "end": v(-0.75, 64.25) * mm, "construction": true});
            skLineSegment(sketch, "E17.0.5.4", {"start": v(5.75, 70.75) * mm, "end": v(-0.75, 70.75) * mm, "construction": true});
            skCircle(sketch, "E17.0.5.5", {"center": v(-0.75, 64.25) * mm, "radius": 1.3 * mm});
            skCircle(sketch, "E17.0.5.6", {"center": v(5.75, 64.25) * mm, "radius": 1.3 * mm});
            skCircle(sketch, "E17.0.5.7", {"center": v(5.75, 70.75) * mm, "radius": 1.3 * mm});
            skCircle(sketch, "E17.0.5.8", {"center": v(-0.75, 70.75) * mm, "radius": 1.3 * mm});
            skPoint(sketch, "E17.1.0.0", {"position": v(15.5, 2.5) * mm});
            skLineSegment(sketch, "E17.1.0.1", {"start": v(12.25, -0.75) * mm, "end": v(12.25, 5.75) * mm, "construction": true});
            skLineSegment(sketch, "E17.1.0.2", {"start": v(18.75, -0.75) * mm, "end": v(18.75, 5.75) * mm, "construction": true});
            skLineSegment(sketch, "E17.1.0.3", {"start": v(18.75, -0.75) * mm, "end": v(12.25, -0.75) * mm, "construction": true});
            skLineSegment(sketch, "E17.1.0.4", {"start": v(18.75, 5.75) * mm, "end": v(12.25, 5.75) * mm, "construction": true});
            skCircle(sketch, "E17.1.0.5", {"center": v(12.25, -0.75) * mm, "radius": 1.3 * mm});
            skCircle(sketch, "E17.1.0.6", {"center": v(18.75, -0.75) * mm, "radius": 1.3 * mm});
            skCircle(sketch, "E17.1.0.7", {"center": v(18.75, 5.75) * mm, "radius": 1.3 * mm});
            skCircle(sketch, "E17.1.0.8", {"center": v(12.25, 5.75) * mm, "radius": 1.3 * mm});
            skPoint(sketch, "E17.1.1.0", {"position": v(15.5, 15.5) * mm});
            skLineSegment(sketch, "E17.1.1.1", {"start": v(12.25, 12.25) * mm, "end": v(12.25, 18.75) * mm, "construction": true});
            skLineSegment(sketch, "E17.1.1.2", {"start": v(18.75, 12.25) * mm, "end": v(18.75, 18.75) * mm, "construction": true});
            skLineSegment(sketch, "E17.1.1.3", {"start": v(18.75, 12.25) * mm, "end": v(12.25, 12.25) * mm, "construction": true});
            skLineSegment(sketch, "E17.1.1.4", {"start": v(18.75, 18.75) * mm, "end": v(12.25, 18.75) * mm, "construction": true});
            skCircle(sketch, "E17.1.1.5", {"center": v(12.25, 12.25) * mm, "radius": 1.3 * mm});
            skCircle(sketch, "E17.1.1.6", {"center": v(18.75, 12.25) * mm, "radius": 1.3 * mm});
            skCircle(sketch, "E17.1.1.7", {"center": v(18.75, 18.75) * mm, "radius": 1.3 * mm});
            skCircle(sketch, "E17.1.1.8", {"center": v(12.25, 18.75) * mm, "radius": 1.3 * mm});
            skPoint(sketch, "E17.1.2.0", {"position": v(15.5, 28.5) * mm});
            skLineSegment(sketch, "E17.1.2.1", {"start": v(12.25, 25.25) * mm, "end": v(12.25, 31.75) * mm, "construction": true});
            skLineSegment(sketch, "E17.1.2.2", {"start": v(18.75, 25.25) * mm, "end": v(18.75, 31.75) * mm, "construction": true});
            skLineSegment(sketch, "E17.1.2.3", {"start": v(18.75, 25.25) * mm, "end": v(12.25, 25.25) * mm, "construction": true});
            skLineSegment(sketch, "E17.1.2.4", {"start": v(18.75, 31.75) * mm, "end": v(12.25, 31.75) * mm, "construction": true});
            skCircle(sketch, "E17.1.2.5", {"center": v(12.25, 25.25) * mm, "radius": 1.3 * mm});
            skCircle(sketch, "E17.1.2.6", {"center": v(18.75, 25.25) * mm, "radius": 1.3 * mm});
            skCircle(sketch, "E17.1.2.7", {"center": v(18.75, 31.75) * mm, "radius": 1.3 * mm});
            skCircle(sketch, "E17.1.2.8", {"center": v(12.25, 31.75) * mm, "radius": 1.3 * mm});
            skPoint(sketch, "E17.1.3.0", {"position": v(15.5, 41.5) * mm});
            skLineSegment(sketch, "E17.1.3.1", {"start": v(12.25, 38.25) * mm, "end": v(12.25, 44.75) * mm, "construction": true});
            skLineSegment(sketch, "E17.1.3.2", {"start": v(18.75, 38.25) * mm, "end": v(18.75, 44.75) * mm, "construction": true});
            skLineSegment(sketch, "E17.1.3.3", {"start": v(18.75, 38.25) * mm, "end": v(12.25, 38.25) * mm, "construction": true});
            skLineSegment(sketch, "E17.1.3.4", {"start": v(18.75, 44.75) * mm, "end": v(12.25, 44.75) * mm, "construction": true});
            skCircle(sketch, "E17.1.3.5", {"center": v(12.25, 38.25) * mm, "radius": 1.3 * mm});
            skCircle(sketch, "E17.1.3.6", {"center": v(18.75, 38.25) * mm, "radius": 1.3 * mm});
            skCircle(sketch, "E17.1.3.7", {"center": v(18.75, 44.75) * mm, "radius": 1.3 * mm});
            skCircle(sketch, "E17.1.3.8", {"center": v(12.25, 44.75) * mm, "radius": 1.3 * mm});
            skPoint(sketch, "E17.1.4.0", {"position": v(15.5, 54.5) * mm});
            skLineSegment(sketch, "E17.1.4.1", {"start": v(12.25, 51.25) * mm, "end": v(12.25, 57.75) * mm, "construction": true});
            skLineSegment(sketch, "E17.1.4.2", {"start": v(18.75, 51.25) * mm, "end": v(18.75, 57.75) * mm, "construction": true});
            skLineSegment(sketch, "E17.1.4.3", {"start": v(18.75, 51.25) * mm, "end": v(12.25, 51.25) * mm, "construction": true});
            skLineSegment(sketch, "E17.1.4.4", {"start": v(18.75, 57.75) * mm, "end": v(12.25, 57.75) * mm, "construction": true});
            skCircle(sketch, "E17.1.4.5", {"center": v(12.25, 51.25) * mm, "radius": 1.3 * mm});
            skCircle(sketch, "E17.1.4.6", {"center": v(18.75, 51.25) * mm, "radius": 1.3 * mm});
            skCircle(sketch, "E17.1.4.7", {"center": v(18.75, 57.75) * mm, "radius": 1.3 * mm});
            skCircle(sketch, "E17.1.4.8", {"center": v(12.25, 57.75) * mm, "radius": 1.3 * mm});
            skPoint(sketch, "E17.1.5.0", {"position": v(15.5, 67.5) * mm});
            skLineSegment(sketch, "E17.1.5.1", {"start": v(12.25, 64.25) * mm, "end": v(12.25, 70.75) * mm, "construction": true});
            skLineSegment(sketch, "E17.1.5.2", {"start": v(18.75, 64.25) * mm, "end": v(18.75, 70.75) * mm, "construction": true});
            skLineSegment(sketch, "E17.1.5.3", {"start": v(18.75, 64.25) * mm, "end": v(12.25, 64.25) * mm, "construction": true});
            skLineSegment(sketch, "E17.1.5.4", {"start": v(18.75, 70.75) * mm, "end": v(12.25, 70.75) * mm, "construction": true});
            skCircle(sketch, "E17.1.5.5", {"center": v(12.25, 64.25) * mm, "radius": 1.3 * mm});
            skCircle(sketch, "E17.1.5.6", {"center": v(18.75, 64.25) * mm, "radius": 1.3 * mm});
            skCircle(sketch, "E17.1.5.7", {"center": v(18.75, 70.75) * mm, "radius": 1.3 * mm});
            skCircle(sketch, "E17.1.5.8", {"center": v(12.25, 70.75) * mm, "radius": 1.3 * mm});
            skPoint(sketch, "E17.2.0.0", {"position": v(28.5, 2.5) * mm});
            skLineSegment(sketch, "E17.2.0.1", {"start": v(25.25, -0.75) * mm, "end": v(25.25, 5.75) * mm, "construction": true});
            skLineSegment(sketch, "E17.2.0.2", {"start": v(31.75, -0.75) * mm, "end": v(31.75, 5.75) * mm, "construction": true});
            skLineSegment(sketch, "E17.2.0.3", {"start": v(31.75, -0.75) * mm, "end": v(25.25, -0.75) * mm, "construction": true});
            skLineSegment(sketch, "E17.2.0.4", {"start": v(31.75, 5.75) * mm, "end": v(25.25, 5.75) * mm, "construction": true});
            skCircle(sketch, "E17.2.0.5", {"center": v(25.25, -0.75) * mm, "radius": 1.3 * mm});
            skCircle(sketch, "E17.2.0.6", {"center": v(31.75, -0.75) * mm, "radius": 1.3 * mm});
            skCircle(sketch, "E17.2.0.7", {"center": v(31.75, 5.75) * mm, "radius": 1.3 * mm});
            skCircle(sketch, "E17.2.0.8", {"center": v(25.25, 5.75) * mm, "radius": 1.3 * mm});
            skPoint(sketch, "E17.2.1.0", {"position": v(28.5, 15.5) * mm});
            skLineSegment(sketch, "E17.2.1.1", {"start": v(25.25, 12.25) * mm, "end": v(25.25, 18.75) * mm, "construction": true});
            skLineSegment(sketch, "E17.2.1.2", {"start": v(31.75, 12.25) * mm, "end": v(31.75, 18.75) * mm, "construction": true});
            skLineSegment(sketch, "E17.2.1.3", {"start": v(31.75, 12.25) * mm, "end": v(25.25, 12.25) * mm, "construction": true});
            skLineSegment(sketch, "E17.2.1.4", {"start": v(31.75, 18.75) * mm, "end": v(25.25, 18.75) * mm, "construction": true});
            skCircle(sketch, "E17.2.1.5", {"center": v(25.25, 12.25) * mm, "radius": 1.3 * mm});
            skCircle(sketch, "E17.2.1.6", {"center": v(31.75, 12.25) * mm, "radius": 1.3 * mm});
            skCircle(sketch, "E17.2.1.7", {"center": v(31.75, 18.75) * mm, "radius": 1.3 * mm});
            skCircle(sketch, "E17.2.1.8", {"center": v(25.25, 18.75) * mm, "radius": 1.3 * mm});
            skPoint(sketch, "E17.2.2.0", {"position": v(28.5, 28.5) * mm});
            skLineSegment(sketch, "E17.2.2.1", {"start": v(25.25, 25.25) * mm, "end": v(25.25, 31.75) * mm, "construction": true});
            skLineSegment(sketch, "E17.2.2.2", {"start": v(31.75, 25.25) * mm, "end": v(31.75, 31.75) * mm, "construction": true});
            skLineSegment(sketch, "E17.2.2.3", {"start": v(31.75, 25.25) * mm, "end": v(25.25, 25.25) * mm, "construction": true});
            skLineSegment(sketch, "E17.2.2.4", {"start": v(31.75, 31.75) * mm, "end": v(25.25, 31.75) * mm, "construction": true});
            skCircle(sketch, "E17.2.2.5", {"center": v(25.25, 25.25) * mm, "radius": 1.3 * mm});
            skCircle(sketch, "E17.2.2.6", {"center": v(31.75, 25.25) * mm, "radius": 1.3 * mm});
            skCircle(sketch, "E17.2.2.7", {"center": v(31.75, 31.75) * mm, "radius": 1.3 * mm});
            skCircle(sketch, "E17.2.2.8", {"center": v(25.25, 31.75) * mm, "radius": 1.3 * mm});
            skPoint(sketch, "E17.2.3.0", {"position": v(28.5, 41.5) * mm});
            skLineSegment(sketch, "E17.2.3.1", {"start": v(25.25, 38.25) * mm, "end": v(25.25, 44.75) * mm, "construction": true});
            skLineSegment(sketch, "E17.2.3.2", {"start": v(31.75, 38.25) * mm, "end": v(31.75, 44.75) * mm, "construction": true});
            skLineSegment(sketch, "E17.2.3.3", {"start": v(31.75, 38.25) * mm, "end": v(25.25, 38.25) * mm, "construction": true});
            skLineSegment(sketch, "E17.2.3.4", {"start": v(31.75, 44.75) * mm, "end": v(25.25, 44.75) * mm, "construction": true});
            skCircle(sketch, "E17.2.3.5", {"center": v(25.25, 38.25) * mm, "radius": 1.3 * mm});
            skCircle(sketch, "E17.2.3.6", {"center": v(31.75, 38.25) * mm, "radius": 1.3 * mm});
            skCircle(sketch, "E17.2.3.7", {"center": v(31.75, 44.75) * mm, "radius": 1.3 * mm});
            skCircle(sketch, "E17.2.3.8", {"center": v(25.25, 44.75) * mm, "radius": 1.3 * mm});
            skPoint(sketch, "E17.2.4.0", {"position": v(28.5, 54.5) * mm});
            skLineSegment(sketch, "E17.2.4.1", {"start": v(25.25, 51.25) * mm, "end": v(25.25, 57.75) * mm, "construction": true});
            skLineSegment(sketch, "E17.2.4.2", {"start": v(31.75, 51.25) * mm, "end": v(31.75, 57.75) * mm, "construction": true});
            skLineSegment(sketch, "E17.2.4.3", {"start": v(31.75, 51.25) * mm, "end": v(25.25, 51.25) * mm, "construction": true});
            skLineSegment(sketch, "E17.2.4.4", {"start": v(31.75, 57.75) * mm, "end": v(25.25, 57.75) * mm, "construction": true});
            skCircle(sketch, "E17.2.4.5", {"center": v(25.25, 51.25) * mm, "radius": 1.3 * mm});
            skCircle(sketch, "E17.2.4.6", {"center": v(31.75, 51.25) * mm, "radius": 1.3 * mm});
            skCircle(sketch, "E17.2.4.7", {"center": v(31.75, 57.75) * mm, "radius": 1.3 * mm});
            skCircle(sketch, "E17.2.4.8", {"center": v(25.25, 57.75) * mm, "radius": 1.3 * mm});
            skPoint(sketch, "E17.2.5.0", {"position": v(28.5, 67.5) * mm});
            skLineSegment(sketch, "E17.2.5.1", {"start": v(25.25, 64.25) * mm, "end": v(25.25, 70.75) * mm, "construction": true});
            skLineSegment(sketch, "E17.2.5.2", {"start": v(31.75, 64.25) * mm, "end": v(31.75, 70.75) * mm, "construction": true});
            skLineSegment(sketch, "E17.2.5.3", {"start": v(31.75, 64.25) * mm, "end": v(25.25, 64.25) * mm, "construction": true});
            skLineSegment(sketch, "E17.2.5.4", {"start": v(31.75, 70.75) * mm, "end": v(25.25, 70.75) * mm, "construction": true});
            skCircle(sketch, "E17.2.5.5", {"center": v(25.25, 64.25) * mm, "radius": 1.3 * mm});
            skCircle(sketch, "E17.2.5.6", {"center": v(31.75, 64.25) * mm, "radius": 1.3 * mm});
            skCircle(sketch, "E17.2.5.7", {"center": v(31.75, 70.75) * mm, "radius": 1.3 * mm});
            skCircle(sketch, "E17.2.5.8", {"center": v(25.25, 70.75) * mm, "radius": 1.3 * mm});
            skPoint(sketch, "E17.3.0.0", {"position": v(41.5, 2.5) * mm});
            skLineSegment(sketch, "E17.3.0.1", {"start": v(38.25, -0.75) * mm, "end": v(38.25, 5.75) * mm, "construction": true});
            skLineSegment(sketch, "E17.3.0.2", {"start": v(44.75, -0.75) * mm, "end": v(44.75, 5.75) * mm, "construction": true});
            skLineSegment(sketch, "E17.3.0.3", {"start": v(44.75, -0.75) * mm, "end": v(38.25, -0.75) * mm, "construction": true});
            skLineSegment(sketch, "E17.3.0.4", {"start": v(44.75, 5.75) * mm, "end": v(38.25, 5.75) * mm, "construction": true});
            skCircle(sketch, "E17.3.0.5", {"center": v(38.25, -0.75) * mm, "radius": 1.3 * mm});
            skCircle(sketch, "E17.3.0.6", {"center": v(44.75, -0.75) * mm, "radius": 1.3 * mm});
            skCircle(sketch, "E17.3.0.7", {"center": v(44.75, 5.75) * mm, "radius": 1.3 * mm});
            skCircle(sketch, "E17.3.0.8", {"center": v(38.25, 5.75) * mm, "radius": 1.3 * mm});
            skPoint(sketch, "E17.3.1.0", {"position": v(41.5, 15.5) * mm});
            skLineSegment(sketch, "E17.3.1.1", {"start": v(38.25, 12.25) * mm, "end": v(38.25, 18.75) * mm, "construction": true});
            skLineSegment(sketch, "E17.3.1.2", {"start": v(44.75, 12.25) * mm, "end": v(44.75, 18.75) * mm, "construction": true});
            skLineSegment(sketch, "E17.3.1.3", {"start": v(44.75, 12.25) * mm, "end": v(38.25, 12.25) * mm, "construction": true});
            skLineSegment(sketch, "E17.3.1.4", {"start": v(44.75, 18.75) * mm, "end": v(38.25, 18.75) * mm, "construction": true});
            skCircle(sketch, "E17.3.1.5", {"center": v(38.25, 12.25) * mm, "radius": 1.3 * mm});
            skCircle(sketch, "E17.3.1.6", {"center": v(44.75, 12.25) * mm, "radius": 1.3 * mm});
            skCircle(sketch, "E17.3.1.7", {"center": v(44.75, 18.75) * mm, "radius": 1.3 * mm});
            skCircle(sketch, "E17.3.1.8", {"center": v(38.25, 18.75) * mm, "radius": 1.3 * mm});
            skPoint(sketch, "E17.3.2.0", {"position": v(41.5, 28.5) * mm});
            skLineSegment(sketch, "E17.3.2.1", {"start": v(38.25, 25.25) * mm, "end": v(38.25, 31.75) * mm, "construction": true});
            skLineSegment(sketch, "E17.3.2.2", {"start": v(44.75, 25.25) * mm, "end": v(44.75, 31.75) * mm, "construction": true});
            skLineSegment(sketch, "E17.3.2.3", {"start": v(44.75, 25.25) * mm, "end": v(38.25, 25.25) * mm, "construction": true});
            skLineSegment(sketch, "E17.3.2.4", {"start": v(44.75, 31.75) * mm, "end": v(38.25, 31.75) * mm, "construction": true});
            skCircle(sketch, "E17.3.2.5", {"center": v(38.25, 25.25) * mm, "radius": 1.3 * mm});
            skCircle(sketch, "E17.3.2.6", {"center": v(44.75, 25.25) * mm, "radius": 1.3 * mm});
            skCircle(sketch, "E17.3.2.7", {"center": v(44.75, 31.75) * mm, "radius": 1.3 * mm});
            skCircle(sketch, "E17.3.2.8", {"center": v(38.25, 31.75) * mm, "radius": 1.3 * mm});
            skPoint(sketch, "E17.3.3.0", {"position": v(41.5, 41.5) * mm});
            skLineSegment(sketch, "E17.3.3.1", {"start": v(38.25, 38.25) * mm, "end": v(38.25, 44.75) * mm, "construction": true});
            skLineSegment(sketch, "E17.3.3.2", {"start": v(44.75, 38.25) * mm, "end": v(44.75, 44.75) * mm, "construction": true});
            skLineSegment(sketch, "E17.3.3.3", {"start": v(44.75, 38.25) * mm, "end": v(38.25, 38.25) * mm, "construction": true});
            skLineSegment(sketch, "E17.3.3.4", {"start": v(44.75, 44.75) * mm, "end": v(38.25, 44.75) * mm, "construction": true});
            skCircle(sketch, "E17.3.3.5", {"center": v(38.25, 38.25) * mm, "radius": 1.3 * mm});
            skCircle(sketch, "E17.3.3.6", {"center": v(44.75, 38.25) * mm, "radius": 1.3 * mm});
            skCircle(sketch, "E17.3.3.7", {"center": v(44.75, 44.75) * mm, "radius": 1.3 * mm});
            skCircle(sketch, "E17.3.3.8", {"center": v(38.25, 44.75) * mm, "radius": 1.3 * mm});
            skPoint(sketch, "E17.3.4.0", {"position": v(41.5, 54.5) * mm});
            skLineSegment(sketch, "E17.3.4.1", {"start": v(38.25, 51.25) * mm, "end": v(38.25, 57.75) * mm, "construction": true});
            skLineSegment(sketch, "E17.3.4.2", {"start": v(44.75, 51.25) * mm, "end": v(44.75, 57.75) * mm, "construction": true});
            skLineSegment(sketch, "E17.3.4.3", {"start": v(44.75, 51.25) * mm, "end": v(38.25, 51.25) * mm, "construction": true});
            skLineSegment(sketch, "E17.3.4.4", {"start": v(44.75, 57.75) * mm, "end": v(38.25, 57.75) * mm, "construction": true});
            skCircle(sketch, "E17.3.4.5", {"center": v(38.25, 51.25) * mm, "radius": 1.3 * mm});
            skCircle(sketch, "E17.3.4.6", {"center": v(44.75, 51.25) * mm, "radius": 1.3 * mm});
            skCircle(sketch, "E17.3.4.7", {"center": v(44.75, 57.75) * mm, "radius": 1.3 * mm});
            skCircle(sketch, "E17.3.4.8", {"center": v(38.25, 57.75) * mm, "radius": 1.3 * mm});
            skPoint(sketch, "E17.3.5.0", {"position": v(41.5, 67.5) * mm});
            skLineSegment(sketch, "E17.3.5.1", {"start": v(38.25, 64.25) * mm, "end": v(38.25, 70.75) * mm, "construction": true});
            skLineSegment(sketch, "E17.3.5.2", {"start": v(44.75, 64.25) * mm, "end": v(44.75, 70.75) * mm, "construction": true});
            skLineSegment(sketch, "E17.3.5.3", {"start": v(44.75, 64.25) * mm, "end": v(38.25, 64.25) * mm, "construction": true});
            skLineSegment(sketch, "E17.3.5.4", {"start": v(44.75, 70.75) * mm, "end": v(38.25, 70.75) * mm, "construction": true});
            skCircle(sketch, "E17.3.5.5", {"center": v(38.25, 64.25) * mm, "radius": 1.3 * mm});
            skCircle(sketch, "E17.3.5.6", {"center": v(44.75, 64.25) * mm, "radius": 1.3 * mm});
            skCircle(sketch, "E17.3.5.7", {"center": v(44.75, 70.75) * mm, "radius": 1.3 * mm});
            skCircle(sketch, "E17.3.5.8", {"center": v(38.25, 70.75) * mm, "radius": 1.3 * mm});
            skPoint(sketch, "E17.4.0.0", {"position": v(54.5, 2.5) * mm});
            skLineSegment(sketch, "E17.4.0.1", {"start": v(51.25, -0.75) * mm, "end": v(51.25, 5.75) * mm, "construction": true});
            skLineSegment(sketch, "E17.4.0.2", {"start": v(57.75, -0.75) * mm, "end": v(57.75, 5.75) * mm, "construction": true});
            skLineSegment(sketch, "E17.4.0.3", {"start": v(57.75, -0.75) * mm, "end": v(51.25, -0.75) * mm, "construction": true});
            skLineSegment(sketch, "E17.4.0.4", {"start": v(57.75, 5.75) * mm, "end": v(51.25, 5.75) * mm, "construction": true});
            skCircle(sketch, "E17.4.0.5", {"center": v(51.25, -0.75) * mm, "radius": 1.3 * mm});
            skCircle(sketch, "E17.4.0.6", {"center": v(57.75, -0.75) * mm, "radius": 1.3 * mm});
            skCircle(sketch, "E17.4.0.7", {"center": v(57.75, 5.75) * mm, "radius": 1.3 * mm});
            skCircle(sketch, "E17.4.0.8", {"center": v(51.25, 5.75) * mm, "radius": 1.3 * mm});
            skPoint(sketch, "E17.4.1.0", {"position": v(54.5, 15.5) * mm});
            skLineSegment(sketch, "E17.4.1.1", {"start": v(51.25, 12.25) * mm, "end": v(51.25, 18.75) * mm, "construction": true});
            skLineSegment(sketch, "E17.4.1.2", {"start": v(57.75, 12.25) * mm, "end": v(57.75, 18.75) * mm, "construction": true});
            skLineSegment(sketch, "E17.4.1.3", {"start": v(57.75, 12.25) * mm, "end": v(51.25, 12.25) * mm, "construction": true});
            skLineSegment(sketch, "E17.4.1.4", {"start": v(57.75, 18.75) * mm, "end": v(51.25, 18.75) * mm, "construction": true});
            skCircle(sketch, "E17.4.1.5", {"center": v(51.25, 12.25) * mm, "radius": 1.3 * mm});
            skCircle(sketch, "E17.4.1.6", {"center": v(57.75, 12.25) * mm, "radius": 1.3 * mm});
            skCircle(sketch, "E17.4.1.7", {"center": v(57.75, 18.75) * mm, "radius": 1.3 * mm});
            skCircle(sketch, "E17.4.1.8", {"center": v(51.25, 18.75) * mm, "radius": 1.3 * mm});
            skPoint(sketch, "E17.4.2.0", {"position": v(54.5, 28.5) * mm});
            skLineSegment(sketch, "E17.4.2.1", {"start": v(51.25, 25.25) * mm, "end": v(51.25, 31.75) * mm, "construction": true});
            skLineSegment(sketch, "E17.4.2.2", {"start": v(57.75, 25.25) * mm, "end": v(57.75, 31.75) * mm, "construction": true});
            skLineSegment(sketch, "E17.4.2.3", {"start": v(57.75, 25.25) * mm, "end": v(51.25, 25.25) * mm, "construction": true});
            skLineSegment(sketch, "E17.4.2.4", {"start": v(57.75, 31.75) * mm, "end": v(51.25, 31.75) * mm, "construction": true});
            skCircle(sketch, "E17.4.2.5", {"center": v(51.25, 25.25) * mm, "radius": 1.3 * mm});
            skCircle(sketch, "E17.4.2.6", {"center": v(57.75, 25.25) * mm, "radius": 1.3 * mm});
            skCircle(sketch, "E17.4.2.7", {"center": v(57.75, 31.75) * mm, "radius": 1.3 * mm});
            skCircle(sketch, "E17.4.2.8", {"center": v(51.25, 31.75) * mm, "radius": 1.3 * mm});
            skPoint(sketch, "E17.4.3.0", {"position": v(54.5, 41.5) * mm});
            skLineSegment(sketch, "E17.4.3.1", {"start": v(51.25, 38.25) * mm, "end": v(51.25, 44.75) * mm, "construction": true});
            skLineSegment(sketch, "E17.4.3.2", {"start": v(57.75, 38.25) * mm, "end": v(57.75, 44.75) * mm, "construction": true});
            skLineSegment(sketch, "E17.4.3.3", {"start": v(57.75, 38.25) * mm, "end": v(51.25, 38.25) * mm, "construction": true});
            skLineSegment(sketch, "E17.4.3.4", {"start": v(57.75, 44.75) * mm, "end": v(51.25, 44.75) * mm, "construction": true});
            skCircle(sketch, "E17.4.3.5", {"center": v(51.25, 38.25) * mm, "radius": 1.3 * mm});
            skCircle(sketch, "E17.4.3.6", {"center": v(57.75, 38.25) * mm, "radius": 1.3 * mm});
            skCircle(sketch, "E17.4.3.7", {"center": v(57.75, 44.75) * mm, "radius": 1.3 * mm});
            skCircle(sketch, "E17.4.3.8", {"center": v(51.25, 44.75) * mm, "radius": 1.3 * mm});
            skPoint(sketch, "E17.4.4.0", {"position": v(54.5, 54.5) * mm});
            skLineSegment(sketch, "E17.4.4.1", {"start": v(51.25, 51.25) * mm, "end": v(51.25, 57.75) * mm, "construction": true});
            skLineSegment(sketch, "E17.4.4.2", {"start": v(57.75, 51.25) * mm, "end": v(57.75, 57.75) * mm, "construction": true});
            skLineSegment(sketch, "E17.4.4.3", {"start": v(57.75, 51.25) * mm, "end": v(51.25, 51.25) * mm, "construction": true});
            skLineSegment(sketch, "E17.4.4.4", {"start": v(57.75, 57.75) * mm, "end": v(51.25, 57.75) * mm, "construction": true});
            skCircle(sketch, "E17.4.4.5", {"center": v(51.25, 51.25) * mm, "radius": 1.3 * mm});
            skCircle(sketch, "E17.4.4.6", {"center": v(57.75, 51.25) * mm, "radius": 1.3 * mm});
            skCircle(sketch, "E17.4.4.7", {"center": v(57.75, 57.75) * mm, "radius": 1.3 * mm});
            skCircle(sketch, "E17.4.4.8", {"center": v(51.25, 57.75) * mm, "radius": 1.3 * mm});
            skPoint(sketch, "E17.4.5.0", {"position": v(54.5, 67.5) * mm});
            skLineSegment(sketch, "E17.4.5.1", {"start": v(51.25, 64.25) * mm, "end": v(51.25, 70.75) * mm, "construction": true});
            skLineSegment(sketch, "E17.4.5.2", {"start": v(57.75, 64.25) * mm, "end": v(57.75, 70.75) * mm, "construction": true});
            skLineSegment(sketch, "E17.4.5.3", {"start": v(57.75, 64.25) * mm, "end": v(51.25, 64.25) * mm, "construction": true});
            skLineSegment(sketch, "E17.4.5.4", {"start": v(57.75, 70.75) * mm, "end": v(51.25, 70.75) * mm, "construction": true});
            skCircle(sketch, "E17.4.5.5", {"center": v(51.25, 64.25) * mm, "radius": 1.3 * mm});
            skCircle(sketch, "E17.4.5.6", {"center": v(57.75, 64.25) * mm, "radius": 1.3 * mm});
            skCircle(sketch, "E17.4.5.7", {"center": v(57.75, 70.75) * mm, "radius": 1.3 * mm});
            skCircle(sketch, "E17.4.5.8", {"center": v(51.25, 70.75) * mm, "radius": 1.3 * mm});
            skPoint(sketch, "E17.5.0.0", {"position": v(67.5, 2.5) * mm});
            skLineSegment(sketch, "E17.5.0.1", {"start": v(64.25, -0.75) * mm, "end": v(64.25, 5.75) * mm, "construction": true});
            skLineSegment(sketch, "E17.5.0.2", {"start": v(70.75, -0.75) * mm, "end": v(70.75, 5.75) * mm, "construction": true});
            skLineSegment(sketch, "E17.5.0.3", {"start": v(70.75, -0.75) * mm, "end": v(64.25, -0.75) * mm, "construction": true});
            skLineSegment(sketch, "E17.5.0.4", {"start": v(70.75, 5.75) * mm, "end": v(64.25, 5.75) * mm, "construction": true});
            skCircle(sketch, "E17.5.0.5", {"center": v(64.25, -0.75) * mm, "radius": 1.3 * mm});
            skCircle(sketch, "E17.5.0.6", {"center": v(70.75, -0.75) * mm, "radius": 1.3 * mm});
            skCircle(sketch, "E17.5.0.7", {"center": v(70.75, 5.75) * mm, "radius": 1.3 * mm});
            skCircle(sketch, "E17.5.0.8", {"center": v(64.25, 5.75) * mm, "radius": 1.3 * mm});
            skPoint(sketch, "E17.5.1.0", {"position": v(67.5, 15.5) * mm});
            skLineSegment(sketch, "E17.5.1.1", {"start": v(64.25, 12.25) * mm, "end": v(64.25, 18.75) * mm, "construction": true});
            skLineSegment(sketch, "E17.5.1.2", {"start": v(70.75, 12.25) * mm, "end": v(70.75, 18.75) * mm, "construction": true});
            skLineSegment(sketch, "E17.5.1.3", {"start": v(70.75, 12.25) * mm, "end": v(64.25, 12.25) * mm, "construction": true});
            skLineSegment(sketch, "E17.5.1.4", {"start": v(70.75, 18.75) * mm, "end": v(64.25, 18.75) * mm, "construction": true});
            skCircle(sketch, "E17.5.1.5", {"center": v(64.25, 12.25) * mm, "radius": 1.3 * mm});
            skCircle(sketch, "E17.5.1.6", {"center": v(70.75, 12.25) * mm, "radius": 1.3 * mm});
            skCircle(sketch, "E17.5.1.7", {"center": v(70.75, 18.75) * mm, "radius": 1.3 * mm});
            skCircle(sketch, "E17.5.1.8", {"center": v(64.25, 18.75) * mm, "radius": 1.3 * mm});
            skPoint(sketch, "E17.5.2.0", {"position": v(67.5, 28.5) * mm});
            skLineSegment(sketch, "E17.5.2.1", {"start": v(64.25, 25.25) * mm, "end": v(64.25, 31.75) * mm, "construction": true});
            skLineSegment(sketch, "E17.5.2.2", {"start": v(70.75, 25.25) * mm, "end": v(70.75, 31.75) * mm, "construction": true});
            skLineSegment(sketch, "E17.5.2.3", {"start": v(70.75, 25.25) * mm, "end": v(64.25, 25.25) * mm, "construction": true});
            skLineSegment(sketch, "E17.5.2.4", {"start": v(70.75, 31.75) * mm, "end": v(64.25, 31.75) * mm, "construction": true});
            skCircle(sketch, "E17.5.2.5", {"center": v(64.25, 25.25) * mm, "radius": 1.3 * mm});
            skCircle(sketch, "E17.5.2.6", {"center": v(70.75, 25.25) * mm, "radius": 1.3 * mm});
            skCircle(sketch, "E17.5.2.7", {"center": v(70.75, 31.75) * mm, "radius": 1.3 * mm});
            skCircle(sketch, "E17.5.2.8", {"center": v(64.25, 31.75) * mm, "radius": 1.3 * mm});
            skPoint(sketch, "E17.5.3.0", {"position": v(67.5, 41.5) * mm});
            skLineSegment(sketch, "E17.5.3.1", {"start": v(64.25, 38.25) * mm, "end": v(64.25, 44.75) * mm, "construction": true});
            skLineSegment(sketch, "E17.5.3.2", {"start": v(70.75, 38.25) * mm, "end": v(70.75, 44.75) * mm, "construction": true});
            skLineSegment(sketch, "E17.5.3.3", {"start": v(70.75, 38.25) * mm, "end": v(64.25, 38.25) * mm, "construction": true});
            skLineSegment(sketch, "E17.5.3.4", {"start": v(70.75, 44.75) * mm, "end": v(64.25, 44.75) * mm, "construction": true});
            skCircle(sketch, "E17.5.3.5", {"center": v(64.25, 38.25) * mm, "radius": 1.3 * mm});
            skCircle(sketch, "E17.5.3.6", {"center": v(70.75, 38.25) * mm, "radius": 1.3 * mm});
            skCircle(sketch, "E17.5.3.7", {"center": v(70.75, 44.75) * mm, "radius": 1.3 * mm});
            skCircle(sketch, "E17.5.3.8", {"center": v(64.25, 44.75) * mm, "radius": 1.3 * mm});
            skPoint(sketch, "E17.5.4.0", {"position": v(67.5, 54.5) * mm});
            skLineSegment(sketch, "E17.5.4.1", {"start": v(64.25, 51.25) * mm, "end": v(64.25, 57.75) * mm, "construction": true});
            skLineSegment(sketch, "E17.5.4.2", {"start": v(70.75, 51.25) * mm, "end": v(70.75, 57.75) * mm, "construction": true});
            skLineSegment(sketch, "E17.5.4.3", {"start": v(70.75, 51.25) * mm, "end": v(64.25, 51.25) * mm, "construction": true});
            skLineSegment(sketch, "E17.5.4.4", {"start": v(70.75, 57.75) * mm, "end": v(64.25, 57.75) * mm, "construction": true});
            skCircle(sketch, "E17.5.4.5", {"center": v(64.25, 51.25) * mm, "radius": 1.3 * mm});
            skCircle(sketch, "E17.5.4.6", {"center": v(70.75, 51.25) * mm, "radius": 1.3 * mm});
            skCircle(sketch, "E17.5.4.7", {"center": v(70.75, 57.75) * mm, "radius": 1.3 * mm});
            skCircle(sketch, "E17.5.4.8", {"center": v(64.25, 57.75) * mm, "radius": 1.3 * mm});
            skPoint(sketch, "E17.5.5.0", {"position": v(67.5, 67.5) * mm});
            skLineSegment(sketch, "E17.5.5.1", {"start": v(64.25, 64.25) * mm, "end": v(64.25, 70.75) * mm, "construction": true});
            skLineSegment(sketch, "E17.5.5.2", {"start": v(70.75, 64.25) * mm, "end": v(70.75, 70.75) * mm, "construction": true});
            skLineSegment(sketch, "E17.5.5.3", {"start": v(70.75, 64.25) * mm, "end": v(64.25, 64.25) * mm, "construction": true});
            skLineSegment(sketch, "E17.5.5.4", {"start": v(70.75, 70.75) * mm, "end": v(64.25, 70.75) * mm, "construction": true});
            skCircle(sketch, "E17.5.5.5", {"center": v(64.25, 64.25) * mm, "radius": 1.3 * mm});
            skCircle(sketch, "E17.5.5.6", {"center": v(70.75, 64.25) * mm, "radius": 1.3 * mm});
            skCircle(sketch, "E17.5.5.7", {"center": v(70.75, 70.75) * mm, "radius": 1.3 * mm});
            skCircle(sketch, "E17.5.5.8", {"center": v(64.25, 70.75) * mm, "radius": 1.3 * mm});
            skLineSegment(sketch, "E17.direction1", {"start": v(-0.75, -0.75) * mm, "end": v(12.25, -0.75) * mm, "construction": true});
            skLineSegment(sketch, "E17.direction2", {"start": v(-0.75, -0.75) * mm, "end": v(-0.75, 12.25) * mm, "construction": true});
            skLineSegment(sketch, "E18.bottom", {"start": v(-5.75, -5.75) * mm, "end": v(75.75, -5.75) * mm});
            skLineSegment(sketch, "E18.top", {"start": v(-5.75, 75.75) * mm, "end": v(75.75, 75.75) * mm});
            skLineSegment(sketch, "E18.left", {"start": v(-5.75, -5.75) * mm, "end": v(-5.75, 75.75) * mm});
            skLineSegment(sketch, "E18.right", {"start": v(75.75, -5.75) * mm, "end": v(75.75, 75.75) * mm});
            skSolve(sketch);
        }
        {
            var Q0;
            Q0=makeQuery(id+"F4.imprint","IMPRINT",FACE,{"disambiguationData":[TD([[makeQuery(id+"F4.imprint","IMPRINT",EDGE,{"derivedFrom":sQuery(id+"F4.wireOp",EDGE,"E17.0.2.5")}),-1.0]])]});
            extrude(context, id + "F5", {"entities" : qUnion([Q0]), "operationType" : NewBodyOperationType.ADD, "depth" : 2.4 * mm});
        }
    });
